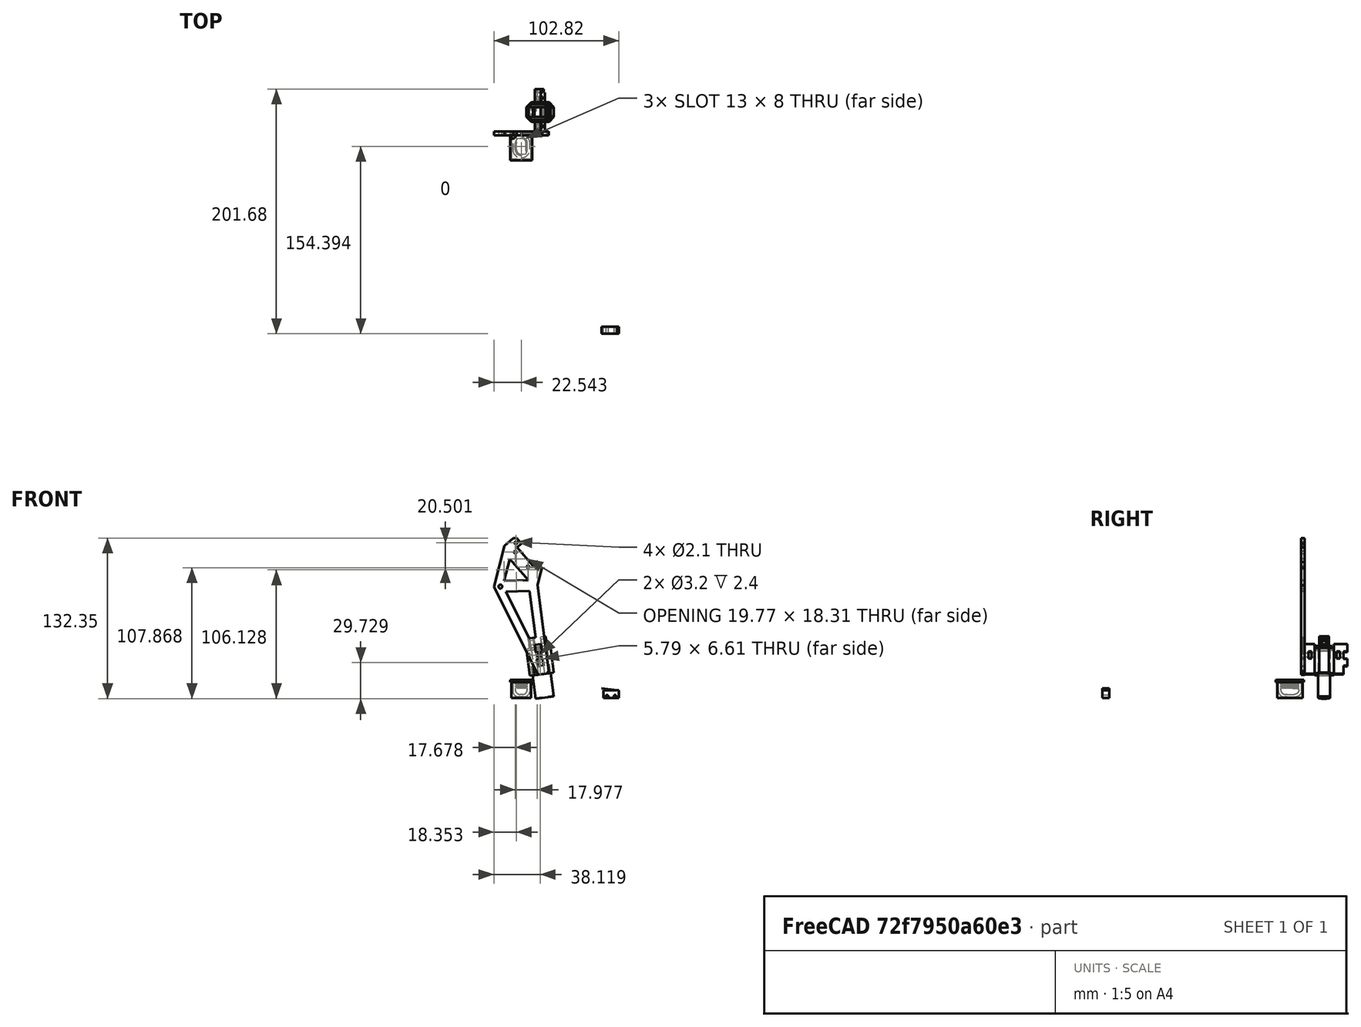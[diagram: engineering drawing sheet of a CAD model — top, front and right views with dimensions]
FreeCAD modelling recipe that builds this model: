
FCSTD DOCUMENT  (FreeCAD 0.19R24276 (Git))
Label: leg_redesigned
License: All rights reserved
LicenseURL: http://en.wikipedia.org/wiki/All_rights_reserved
objects: Sketcher::SketchObject×40, PartDesign::Pocket×30, PartDesign::Pad×19, PartDesign::Chamfer×10, PartDesign::Body×7, PartDesign::Plane×7, PartDesign::ShapeBinder×6, PartDesign::Fillet×6, Mesh::Feature×5, Part::Feature×4, PartDesign::FeatureBase×1
note: 195 computed .brp shape members not serialized (recipe doc carries the construction recipe); baked Part::Feature solids carry a one-line shape summary decoded from their .brp

FEATURE [Mesh::Feature] Component003  label="left_part_original"
FEATURE [Mesh::Feature] Component004  label="right_part_original"
FEATURE [Mesh::Feature] Component005  label="mid_part_original"
FEATURE [Part::Feature] Component004001  label="right_part_original_shape"
  shape: bbox 45.1 x 3 x 112.7 mm, 1032 faces, 0 solids (baked)
FEATURE [Part::Feature] Component003001  label="left_part_original_shape"
  shape: bbox 45.1 x 3 x 112.7 mm, 1032 faces, 0 solids (baked)
FEATURE [PartDesign::ShapeBinder] ShapeBinder
  Support = -> [Component004001]
  TraceSupport = false
FEATURE [PartDesign::ShapeBinder] ShapeBinder001
  Support = -> [Component004001]
  TraceSupport = false
FEATURE [PartDesign::ShapeBinder] ShapeBinder002
  Support = -> [Component003001]
  TraceSupport = false
FEATURE [Sketcher::SketchObject] Sketch
  ExternalGeometry = -> [ShapeBinder,ShapeBinder001,ShapeBinder002]
  FullyConstrained = true
  MapMode = 5
  Placement = pos=(-44.9291,5e-16,-5.90422) rot=(-0.600901,0.600901,0.527102;4.11178rad)
  Support = -> [ShapeBinder]
  sketch-geometry (18):
    g0: LineSegment StartX=-198.684 StartY=38.8278 StartZ=0 EndX=-201.684 EndY=38.8278 EndZ=0
    g1: LineSegment StartX=-198.684 StartY=38.8278 StartZ=0 EndX=-198.684 EndY=44.8278 EndZ=0
    g2: LineSegment StartX=-198.684 StartY=44.8278 StartZ=0 EndX=-201.684 EndY=44.8278 EndZ=0
    g3: LineSegment StartX=-201.684 StartY=44.8278 StartZ=0 EndX=-201.684 EndY=50.8278 EndZ=0
    g4: LineSegment StartX=-201.684 StartY=50.8278 StartZ=0 EndX=-198.684 EndY=50.8278 EndZ=0
    g5: LineSegment StartX=-198.684 StartY=50.8278 StartZ=0 EndX=-166.684 EndY=50.8278 EndZ=0
    g6: LineSegment StartX=-166.684 StartY=50.8278 StartZ=0 EndX=-163.684 EndY=50.8278 EndZ=0
    g7: LineSegment StartX=-163.684 StartY=50.8278 StartZ=0 EndX=-163.684 EndY=44.8278 EndZ=0
    g8: LineSegment StartX=-163.684 StartY=44.8278 StartZ=0 EndX=-166.684 EndY=44.8278 EndZ=0
    g9: LineSegment StartX=-166.684 StartY=44.8278 StartZ=0 EndX=-166.684 EndY=38.8278 EndZ=0
    g10: LineSegment StartX=-166.684 StartY=38.8278 StartZ=0 EndX=-163.684 EndY=38.8278 EndZ=0
    g11: LineSegment StartX=-163.684 StartY=38.8278 StartZ=0 EndX=-163.684 EndY=32.8278 EndZ=0
    g12: LineSegment StartX=-163.684 StartY=32.8278 StartZ=0 EndX=-166.684 EndY=32.8278 EndZ=0
    g13: LineSegment StartX=-201.684 StartY=32.8278 StartZ=0 EndX=-201.684 EndY=38.8278 EndZ=0
    g14: LineSegment StartX=-166.684 StartY=32.8278 StartZ=0 EndX=-166.684 EndY=26.1412 EndZ=0
    g15: LineSegment StartX=-166.684 StartY=26.1412 StartZ=0 EndX=-198.684 EndY=26.1412 EndZ=0
    g16: LineSegment StartX=-198.684 StartY=26.1412 StartZ=0 EndX=-198.684 EndY=32.8278 EndZ=0
    g17: LineSegment StartX=-201.684 StartY=32.8278 StartZ=0 EndX=-198.684 EndY=32.8278 EndZ=0
  constraints (40):
    c: Coincident(g0,g-3)
    c: Coincident(g0,g-4)
    c: Coincident(g1,g0)
    c: Coincident(g1,g-5)
    c: Coincident(g2,g-6)
    c: Coincident(g3,g2)
    c: Vertical(g3)
    c: Coincident(g4,g3)
    c: Coincident(g4,g-6)
    c: Horizontal(g4)
    c: Coincident(g5,g4)
    c: Coincident(g5,g-10)
    c: Coincident(g6,g5)
    c: Coincident(g6,g-9)
    c: Coincident(g7,g6)
    c: Vertical(g7)
    c: Coincident(g8,g7)
    c: Coincident(g8,g-10)
    c: Horizontal(g8)
    c: Coincident(g9,g8)
    c: Coincident(g9,g-8)
    c: Coincident(g10,g9)
    c: Coincident(g10,g-7)
    c: Coincident(g11,g10)
    c: Vertical(g11)
    c: Coincident(g12,g11)
    c: Horizontal(g12)
    c: Coincident(g12,g-8)
    c: Coincident(g13,g0)
    c: Coincident(g1,g2)
    c: Coincident(g14,g12)
    c: Coincident(g15,g14)
    c: Coincident(g-12,g14)
    c: Coincident(g-11,g15)
    c: Coincident(g16,g15)
    c: Vertical(g16)
    c: Coincident(g17,g13)
    c: Horizontal(g17)
    c: Coincident(g16,g17)
    c: Coincident(g-4,g13)
FEATURE [PartDesign::Pad] Pad
  Direction = (1,1,1)
  Length = 5
  Length2 = 100
  Profile = -> Sketch
  Type = 0
FEATURE [Sketcher::SketchObject] Sketch002
  ExternalGeometry = -> [Pad]
  FullyConstrained = true
  MapMode = 5
  Placement = pos=(-6.62244,0,50.3945) rot=(0,-1,0;0.130663rad)
  Support = -> [Pad]
  sketch-geometry (8):
    g0: GeomPoint X=-45.3154 Y=182.684 Z=0
    g1: LineSegment StartX=-57.8154 StartY=190.684 StartZ=0 EndX=-37.8154 EndY=190.684 EndZ=0
    g2: LineSegment StartX=-37.8154 StartY=190.684 StartZ=0 EndX=-37.8154 EndY=174.684 EndZ=0
    g3: LineSegment StartX=-37.8154 StartY=174.684 StartZ=0 EndX=-57.8154 EndY=174.684 EndZ=0
    g4: LineSegment StartX=-57.8154 StartY=174.684 StartZ=0 EndX=-57.8154 EndY=190.684 EndZ=0
    g5: LineSegment StartX=-50.3154 StartY=174.684 StartZ=0 EndX=-45.3154 EndY=174.684 EndZ=0
    g6: GeomPoint X=-47.8154 Y=174.684 Z=0
    g7: LineSegment StartX=-45.3154 StartY=182.684 StartZ=0 EndX=-37.8154 EndY=182.684 EndZ=0
  constraints (19):
    c: Symmetric(g-7,g-10,g0)
    c: Coincident(g1,g2)
    c: Coincident(g2,g3)
    c: Coincident(g3,g4)
    c: Coincident(g4,g1)
    c: Horizontal(g1)
    c: Vertical(g2)
    c: Vertical(g4)
    c: PointOnObject(g5,g-3)
    c: PointOnObject(g5,g-4)
    c: Symmetric(g5,g5,g6)
    c: Symmetric(g3,g2,g6)
    c: Perpendicular(g-3,g5)
    c: Perpendicular(g-3,g3)
    c: Coincident(g7,g0)
    c: Horizontal(g7)
    c: Symmetric(g1,g2,g7)
    c: DistanceX(g1,g1) = 20
    c: DistanceY(g2,g2) = 16
FEATURE [PartDesign::Pad] Pad001
  BaseFeature = -> Pad
  Direction = (1,1,1)
  Length = 24.68
  Length2 = 100
  Profile = -> Sketch002
  Reversed = true
  Type = 0
FEATURE [Sketcher::SketchObject] Sketch003
  ExternalGeometry = -> [Pad001]
  FullyConstrained = true
  MapMode = 5
  Placement = pos=(-6.62244,0,50.3945) rot=(0,-1,0;0.130663rad)
  Support = -> [Pad001]
  sketch-geometry (6):
    g0: ArcOfCircle CenterX=-50.3154 CenterY=182.684 CenterZ=0 NormalX=0 NormalY=0 NormalZ=1 AngleXU=0 Radius=5.2 StartAngle=1.59003 EndAngle=4.71239
    g1: ArcOfCircle CenterX=-45.2144 CenterY=182.684 CenterZ=0 NormalX=0 NormalY=0 NormalZ=1 AngleXU=0 Radius=5.2 StartAngle=4.71239 EndAngle=7.85417
    g2: LineSegment StartX=-50.3154 StartY=177.484 StartZ=0 EndX=-45.2144 EndY=177.484 EndZ=0
    g3: LineSegment StartX=-50.4154 StartY=187.883 StartZ=0 EndX=-45.2154 EndY=187.884 EndZ=0
    g4: LineSegment StartX=-50.3154 StartY=187.883 StartZ=0 EndX=-45.3154 EndY=187.883 EndZ=0
    g5: GeomPoint X=-47.8154 Y=187.883 Z=0
  constraints (14):
    c: Tangent(g0,g2) = -1.5708
    c: Tangent(g2,g1) = -1.5708
    c: Tangent(g3,g1) = 1.5708
    c: Horizontal(g2)
    c: Equal(g0,g1)
    c: DistanceX(g3,g3) = 5.2
    c: Radius(g0) = 5.2
    c: Symmetric(g-9,g-9,g0)
    c: Coincident(g3,g0)
    c: Horizontal(g4)
    c: PointOnObject(g4,g-9)
    c: PointOnObject(g4,g-10)
    c: Symmetric(g4,g4,g5)
    c: Symmetric(g0,g1,g5)
FEATURE [PartDesign::Pocket] Pocket
  BaseFeature = -> Pad001
  Length = 5
  Length2 = 100
  Profile = -> Sketch003
  Type = 1
FEATURE [Sketcher::SketchObject] Sketch004
  ExternalGeometry = -> [Pocket]
  FullyConstrained = true
  MapMode = 5
  Placement = pos=(-5.84069,0,44.4457) rot=(0.997867,0,0.065285;3.14159rad)
  Support = -> [Pocket]
  sketch-geometry (2):
    g0: Circle CenterX=-47.8154 CenterY=-177.104 CenterZ=0 NormalX=0 NormalY=0 NormalZ=1 AngleXU=0 Radius=1.6
    g1: LineSegment StartX=-47.8154 StartY=-178.124 StartZ=0 EndX=-47.8154 EndY=-176.084 EndZ=0
  constraints (5):
    c: PointOnObject(g1,g-6)
    c: Perpendicular(g1,g-4)
    c: Symmetric(g1,g1,g0)
    c: Symmetric(g-4,g-5,g1)
    c: Radius(g0) = 1.6
FEATURE [PartDesign::Pocket] Pocket001
  BaseFeature = -> Pocket
  Length = 8
  Length2 = 100
  Profile = -> Sketch004
  Type = 0
FEATURE [Sketcher::SketchObject] Sketch005
  ExternalGeometry = -> [Pocket001]
  FullyConstrained = false
  MapMode = 5
  Placement = pos=(0,198.684,0) rot=(0,0.707107,0.707107;3.14159rad)
  Support = -> [Pocket001]
  sketch-geometry (2):
    g0: Circle CenterX=52.8734 CenterY=35.2392 CenterZ=0 NormalX=0 NormalY=0 NormalZ=1 AngleXU=0 Radius=1.6
    g1: LineSegment StartX=50.3789 StartY=35.567 StartZ=0 EndX=55.3363 EndY=34.9156 EndZ=0
  constraints (5):
    c: Symmetric(g-5,g-6,g1)
    c: PointOnObject(g1,g-4)
    c: Perpendicular(g1,g-4)
    c: PointOnObject(g0,g1)
    c: Radius(g0) = 1.6
FEATURE [PartDesign::Pocket] Pocket002
  BaseFeature = -> Pocket001
  Length = 8
  Length2 = 100
  Profile = -> Sketch005
  Type = 0
FEATURE [Sketcher::SketchObject] Sketch006
  ExternalGeometry = -> [Pocket002]
  FullyConstrained = false
  MapMode = 5
  Placement = pos=(0,174.684,0) rot=(1,0,0;1.5708rad)
  Support = -> [Pocket002]
  sketch-geometry (14):
    g0: LineSegment StartX=-172.397 StartY=37.8156 StartZ=0 EndX=-169.797 EndY=37.8156 EndZ=0
    g1: LineSegment StartX=-169.797 StartY=37.8156 StartZ=0 EndX=-169.797 EndY=32.0156 EndZ=0
    g2: LineSegment StartX=-169.797 StartY=32.0156 StartZ=0 EndX=-172.397 EndY=32.0156 EndZ=0
    g3: LineSegment StartX=-172.397 StartY=32.0156 StartZ=0 EndX=-172.397 EndY=37.8156 EndZ=0
    g4: LineSegment StartX=-52.7272 StartY=37.8156 StartZ=0 EndX=-50.1272 EndY=37.8156 EndZ=0
    g5: LineSegment StartX=-50.1272 StartY=37.8156 StartZ=0 EndX=-50.1272 EndY=32.0156 EndZ=0
    g6: LineSegment StartX=-50.1272 StartY=32.0156 StartZ=0 EndX=-52.7272 EndY=32.0156 EndZ=0
    g7: LineSegment StartX=-52.7272 StartY=32.0156 StartZ=0 EndX=-52.7272 EndY=37.8156 EndZ=0
    g8: GeomPoint X=87.0771 Y=37.8156 Z=0
    g9: GeomPoint X=-309.601 Y=37.8156 Z=0
    g10: LineSegment StartX=87.0771 StartY=37.8156 StartZ=0 EndX=-309.601 EndY=37.8156 EndZ=0
    g11: GeomPoint X=-111.262 Y=37.8156 Z=0
    g12: GeomPoint X=-55.3363 Y=34.9156 Z=0
    g13: GeomPoint X=-52.7272 Y=34.9156 Z=0
  constraints (31):
    c: Coincident(g0,g1)
    c: Coincident(g1,g2)
    c: Coincident(g2,g3)
    c: Coincident(g3,g0)
    c: Horizontal(g0)
    c: Horizontal(g2)
    c: Vertical(g1)
    c: Vertical(g3)
    c: Coincident(g4,g5)
    c: Coincident(g5,g6)
    c: Coincident(g6,g7)
    c: Coincident(g7,g4)
    c: Horizontal(g4)
    c: Horizontal(g6)
    c: Vertical(g5)
    c: Vertical(g7)
    c: DistanceX(g4,g4) = 2.6
    c: DistanceY(g5,g5) = 5.8
    c: Equal(g0,g4)
    c: Equal(g1,g5)
    c: Horizontal(g2,g5)
    c: PointOnObject(g8,g-7)
    c: DistanceX(g-9,g4) = 3
    c: Coincident(g10,g8)
    c: Coincident(g10,g9)
    c: Horizontal(g10)
    c: Symmetric(g8,g9,g11)
    c: Symmetric(g4,g0,g11)
    c: Symmetric(g-9,g-10,g12)
    c: Symmetric(g4,g6,g13)
    c: Horizontal(g12,g13)
FEATURE [PartDesign::Pocket] Pocket003
  BaseFeature = -> Pocket002
  Length = 5
  Length2 = 100
  Profile = -> Sketch006
  Type = 1
FEATURE [PartDesign::Chamfer] Chamfer
  Angle = 45
  Base = -> Pocket003 [Edge102,Edge66,Edge77,Edge50]
  BaseFeature = -> Pocket003
  ChamferType = 0
  FlipDirection = false
  Size = 4
  Size2 = 1
  SupportTransform = false
FEATURE [Sketcher::SketchObject] Sketch008
  FullyConstrained = false
  MapMode = 5
  Placement = pos=(-6.62244,0,50.3945) rot=(0,-1,0;0.130663rad)
  sketch-geometry (11):
    g0: LineSegment StartX=-57.8154 StartY=186.684 StartZ=0 EndX=-53.8154 EndY=190.684 EndZ=0
    g1: LineSegment StartX=-53.8154 StartY=190.684 StartZ=0 EndX=-44.3154 EndY=190.684 EndZ=0
    g2: LineSegment StartX=-44.3154 StartY=190.684 StartZ=0 EndX=-41.8154 EndY=190.684 EndZ=0
    g3: LineSegment StartX=-41.8154 StartY=190.684 StartZ=0 EndX=-37.8154 EndY=186.684 EndZ=0
    g4: LineSegment StartX=-37.8154 StartY=186.684 StartZ=0 EndX=-37.8154 EndY=178.684 EndZ=0
    g5: LineSegment StartX=-37.8154 StartY=178.684 StartZ=0 EndX=-41.8154 EndY=174.684 EndZ=0
    g6: LineSegment StartX=-41.8154 StartY=174.684 StartZ=0 EndX=-44.3154 EndY=174.684 EndZ=0
    g7: LineSegment StartX=-44.3154 StartY=174.684 StartZ=0 EndX=-51.3154 EndY=174.684 EndZ=0
    g8: LineSegment StartX=-51.3154 StartY=174.684 StartZ=0 EndX=-53.8154 EndY=174.684 EndZ=0
    g9: LineSegment StartX=-53.8154 StartY=174.684 StartZ=0 EndX=-57.8154 EndY=178.684 EndZ=0
    g10: LineSegment StartX=-57.8154 StartY=178.684 StartZ=0 EndX=-57.8154 EndY=186.684 EndZ=0
  constraints (11):
    c: Coincident(g1,g0)
    c: Coincident(g3,g2)
    c: Coincident(g4,g3)
    c: Coincident(g5,g4)
    c: Coincident(g6,g5)
    c: Coincident(g7,g6)
    c: Coincident(g9,g8)
    c: Coincident(g10,g0)
    c: Coincident(g2,g1)
    c: Coincident(g10,g9)
    c: Coincident(g8,g7)
FEATURE [PartDesign::Pocket] Pocket004
  BaseFeature = -> Chamfer
  Length = 4
  Length2 = 100
  Profile = -> Sketch008
  Type = 0
FEATURE [PartDesign::ShapeBinder] ShapeBinder003
  Support = -> [Pocket004]
  TraceSupport = false
FEATURE [Sketcher::SketchObject] Sketch009
  ExternalGeometry = -> [ShapeBinder003]
  FullyConstrained = true
  MapMode = 5
  Placement = pos=(-6.10127,5e-16,46.4286) rot=(0,-1,0;0.130663rad)
  Support = -> [ShapeBinder003]
  sketch-geometry (4):
    g0: ArcOfCircle CenterX=-50.3154 CenterY=182.684 CenterZ=0 NormalX=0 NormalY=0 NormalZ=1 AngleXU=0 Radius=5 StartAngle=1.5708 EndAngle=4.71239
    g1: ArcOfCircle CenterX=-45.3154 CenterY=182.684 CenterZ=0 NormalX=0 NormalY=0 NormalZ=1 AngleXU=0 Radius=5 StartAngle=4.71239 EndAngle=7.85398
    g2: LineSegment StartX=-50.3154 StartY=177.684 StartZ=0 EndX=-45.3154 EndY=177.684 EndZ=0
    g3: LineSegment StartX=-50.3154 StartY=187.684 StartZ=0 EndX=-45.3154 EndY=187.684 EndZ=0
  constraints (7):
    c: Tangent(g0,g3) = 1.5708
    c: Tangent(g0,g2) = -1.5708
    c: Tangent(g2,g1) = -1.5708
    c: Tangent(g3,g1) = 1.5708
    c: Horizontal(g2)
    c: Coincident(g0,g-4)
    c: Tangent(g1,g-3) = -1.5708
FEATURE [PartDesign::Pad] Pad002
  Direction = (1,1,1)
  Length = 40
  Length2 = 100
  Profile = -> Sketch009
  Reversed = true
  Type = 0
FEATURE [Sketcher::SketchObject] Sketch010
  ExternalGeometry = -> [Pad002,ShapeBinder003]
  FullyConstrained = false
  MapMode = 5
  Placement = pos=(-6.10127,-4.7e-15,46.4286) rot=(0,-1,0;0.130663rad)
  Support = -> [Pad002]
  sketch-geometry (15):
    g0: LineSegment StartX=-50.3154 StartY=182.684 StartZ=0 EndX=-45.3154 EndY=182.684 EndZ=0
    g1: GeomPoint X=-47.8154 Y=182.684 Z=0
    g2: LineSegment StartX=-56.3654 StartY=186.012 StartZ=0 EndX=-53.1441 EndY=189.234 EndZ=0
    g3: LineSegment StartX=-53.1441 StartY=189.234 StartZ=0 EndX=-42.4867 EndY=189.234 EndZ=0
    g4: LineSegment StartX=-42.4867 StartY=189.234 StartZ=0 EndX=-39.2654 EndY=186.012 EndZ=0
    g5: LineSegment StartX=-39.2654 StartY=186.012 StartZ=0 EndX=-39.2654 EndY=179.355 EndZ=0
    g6: LineSegment StartX=-39.2654 StartY=179.355 StartZ=0 EndX=-42.4867 EndY=176.134 EndZ=0
    g7: LineSegment StartX=-42.4867 StartY=176.134 StartZ=0 EndX=-53.1441 EndY=176.134 EndZ=0
    g8: LineSegment StartX=-53.1441 StartY=176.134 StartZ=0 EndX=-56.3654 EndY=179.355 EndZ=0
    g9: LineSegment StartX=-56.3654 StartY=179.355 StartZ=0 EndX=-56.3654 EndY=186.012 EndZ=0
    g10: LineSegment StartX=-47.8154 StartY=190.684 StartZ=0 EndX=-47.8154 EndY=174.684 EndZ=0
    g11: LineSegment StartX=-56.3654 StartY=182.684 StartZ=0 EndX=-39.2654 EndY=182.684 EndZ=0
    g12: GeomPoint X=-47.8154 Y=189.234 Z=0
    g13: GeomPoint X=-47.8154 Y=176.134 Z=0
    g14: LineSegment StartX=-40.8761 StartY=187.623 StartZ=0 EndX=-39.8154 EndY=188.684 EndZ=0
  constraints (37):
    c: Symmetric(g-3,g-4,g1)
    c: Coincident(g3,g2)
    c: Horizontal(g3)
    c: Coincident(g5,g4)
    c: Vertical(g5)
    c: Horizontal(g7)
    c: Coincident(g9,g2)
    c: Vertical(g9)
    c: Equal(g3,g7)
    c: Coincident(g7,g8)
    c: Coincident(g6,g7)
    c: Coincident(g4,g3)
    c: Coincident(g6,g5)
    c: Coincident(g8,g9)
    c: Equal(g2,g4)
    c: Equal(g4,g6)
    c: Equal(g6,g8)
    c: Equal(g9,g5)
    c: Horizontal(g4,g2)
    c: Vertical(g10)
    c: Horizontal(g11)
    c: PointOnObject(g11,g5)
    c: PointOnObject(g11,g9)
    c: Symmetric(g11,g11,g1)
    c: PointOnObject(g10,g-19)
    c: PointOnObject(g10,g-16)
    c: PointOnObject(g13,g7)
    c: PointOnObject(g12,g3)
    c: PointOnObject(g13,g10)
    c: PointOnObject(g12,g10)
    c: Symmetric(g12,g13,g1)
    c: Distance(g4,g-14) = 1.5
    c: Distance(g3,g-14) = 1.5
    c: Symmetric(g-14,g-15,g14)
    c: Symmetric(g3,g4,g14)
    c: Perpendicular(g14,g4)
    c: Distance(g2,g-17) = 1.45
FEATURE [PartDesign::Pad] Pad003
  BaseFeature = -> Pad002
  Direction = (1,1,1)
  Length = 2
  Length2 = 100
  Profile = -> Sketch010
  Type = 0
FEATURE [Mesh::Feature] slider_legacy
FEATURE [Part::Feature] slider_legacy001
  shape: bbox 17.12 x 15 x 43.92 mm, 7930 faces, 0 solids (baked)
FEATURE [Sketcher::SketchObject] Sketch011
  ExternalGeometry = -> [ShapeBinder003]
  FullyConstrained = true
  MapMode = 5
  Placement = pos=(-6.36185,-4.4e-15,48.4116) rot=(0,-1,0;0.130663rad)
  Support = -> [Pad003]
  sketch-geometry (21):
    g0: LineSegment StartX=-50.9654 StartY=186.684 StartZ=0 EndX=-50.9654 EndY=178.684 EndZ=0
    g1: LineSegment StartX=-44.6654 StartY=186.684 StartZ=0 EndX=-44.6654 EndY=178.684 EndZ=0
    g2: LineSegment StartX=-44.6654 StartY=186.684 StartZ=0 EndX=-41.6654 EndY=186.684 EndZ=0
    g3: LineSegment StartX=-44.6654 StartY=178.684 StartZ=0 EndX=-41.6654 EndY=178.684 EndZ=0
    g4: LineSegment StartX=-50.9654 StartY=178.684 StartZ=0 EndX=-53.9654 EndY=178.684 EndZ=0
    g5: LineSegment StartX=-50.9654 StartY=186.684 StartZ=0 EndX=-53.9654 EndY=186.684 EndZ=0
    g6: LineSegment StartX=-47.8154 StartY=190.684 StartZ=0 EndX=-47.8154 EndY=174.684 EndZ=0
    g7: LineSegment StartX=-57.8154 StartY=182.684 StartZ=0 EndX=-37.8154 EndY=182.684 EndZ=0
    g8: GeomPoint X=-47.8154 Y=182.684 Z=0
    g9: GeomPoint X=-47.8154 Y=182.684 Z=0
    g10: GeomPoint X=-44.6654 Y=182.684 Z=0
    g11: GeomPoint X=-47.8154 Y=186.684 Z=0
    g12: ArcOfCircle CenterX=-52.9799 CenterY=184.943 CenterZ=0 NormalX=0 NormalY=0 NormalZ=1 AngleXU=0 Radius=2 StartAngle=2.08605 EndAngle=3.02113
    g13: ArcOfCircle CenterX=-52.9799 CenterY=180.424 CenterZ=0 NormalX=0 NormalY=0 NormalZ=1 AngleXU=0 Radius=2 StartAngle=3.26205 EndAngle=4.19714
    g14: LineSegment StartX=-54.9654 StartY=185.184 StartZ=0 EndX=-54.9654 EndY=180.184 EndZ=0
    g15: GeomPoint X=-54.9654 Y=182.684 Z=0
    g16: GeomPoint X=-54.9654 Y=185.184 Z=0
    g17: GeomPoint X=-54.9654 Y=180.184 Z=0
    g18: LineSegment StartX=-40.6654 StartY=185.184 StartZ=0 EndX=-40.6654 EndY=180.184 EndZ=0
    g19: ArcOfCircle CenterX=-42.6509 CenterY=184.943 CenterZ=0 NormalX=0 NormalY=0 NormalZ=1 AngleXU=0 Radius=2 StartAngle=0.12046 EndAngle=1.05555
    g20: ArcOfCircle CenterX=-42.6509 CenterY=180.424 CenterZ=0 NormalX=0 NormalY=0 NormalZ=1 AngleXU=0 Radius=2 StartAngle=5.22764 EndAngle=6.16273
  constraints (53):
    c: Vertical(g0)
    c: Vertical(g1)
    c: Equal(g0,g1)
    c: Horizontal(g1,g0)
    c: DistanceX(g0,g1) = 6.3
    c: Distance(g0) = 8
    c: Coincident(g2,g1)
    c: Horizontal(g2)
    c: Coincident(g3,g1)
    c: Coincident(g4,g0)
    c: Horizontal(g4)
    c: Coincident(g5,g0)
    c: Horizontal(g5)
    c: Horizontal(g3)
    c: Equal(g4,g5)
    c: Equal(g5,g2)
    c: Equal(g2,g3)
    c: DistanceX(g4,g4) = 3
    c: Vertical(g6)
    c: Horizontal(g7)
    c: PointOnObject(g7,g-3)
    c: PointOnObject(g6,g-6)
    c: Symmetric(g7,g7,g9)
    c: Symmetric(g6,g6,g8)
    c: Symmetric(g-4,g-4,g7)
    c: Symmetric(g-5,g-5,g6)
    c: Symmetric(g1,g1,g10)
    c: PointOnObject(g10,g7)
    c: Symmetric(g0,g1,g11)
    c: PointOnObject(g11,g6)
    c: Coincident(g12,g5)
    c: Coincident(g13,g4)
    c: Vertical(g13,g12)
    c: Equal(g13,g12)
    c: Coincident(g14,g12)
    c: Coincident(g14,g13)
    c: PointOnObject(g15,g7)
    c: Coincident(g16,g12)
    c: Coincident(g17,g13)
    c: Symmetric(g12,g13,g15)
    c: DistanceX(g12,g5) = 1
    c: Vertical(g18)
    c: Coincident(g19,g2)
    c: Coincident(g19,g18)
    c: Coincident(g20,g3)
    c: Coincident(g20,g18)
    c: Horizontal(g18,g13)
    c: Horizontal(g18,g12)
    c: Equal(g12,g19)
    c: Equal(g19,g20)
    c: DistanceY(g14,g14) = 5
    c: DistanceX(g2,g18) = 1
    c: Radius(g12) = 2
FEATURE [PartDesign::Pad] Pad004
  BaseFeature = -> Pad003
  Direction = (1,1,1)
  Length = 8
  Length2 = 100
  Profile = -> Sketch011
  Type = 0
FEATURE [Sketcher::SketchObject] Sketch012
  ExternalGeometry = -> [Pad004]
  FullyConstrained = false
  MapMode = 5
  Placement = pos=(-54.4969,5e-16,-7.16153) rot=(-0.600901,0.600901,0.527102;4.11178rad)
  Support = -> [Pad004]
  sketch-geometry (2):
    g0: ArcOfCircle CenterX=-182.684 CenterY=54.8751 CenterZ=0 NormalX=0 NormalY=0 NormalZ=1 AngleXU=0 Radius=6.54374 StartAngle=4.32038 EndAngle=5.1044
    g1: LineSegment StartX=-185.184 StartY=48.8278 StartZ=0 EndX=-180.184 EndY=48.8278 EndZ=0
  constraints (4):
    c: Coincident(g0,g-3)
    c: Coincident(g0,g-3)
    c: Coincident(g1,g0)
    c: Coincident(g1,g0)
FEATURE [PartDesign::Pocket] Pocket005
  BaseFeature = -> Pad004
  Length = 6.3
  Length2 = 100
  Profile = -> Sketch012
  Reversed = true
  Type = 0
FEATURE [Sketcher::SketchObject] Sketch013
  ExternalGeometry = -> [Pocket005]
  FullyConstrained = false
  MapMode = 5
  Placement = pos=(-54.4969,5e-16,-7.16153) rot=(-0.600901,0.600901,0.527102;4.11178rad)
  Support = -> [Pocket005]
  sketch-geometry (5):
    g0: Circle CenterX=-181.888 CenterY=53.2425 CenterZ=0 NormalX=0 NormalY=0 NormalZ=1 AngleXU=0 Radius=1.7
    g1: LineSegment StartX=-186.684 StartY=52.8278 StartZ=0 EndX=-178.684 EndY=52.8278 EndZ=0
    g2: LineSegment StartX=-182.684 StartY=56.8278 StartZ=0 EndX=-182.684 EndY=48.8278 EndZ=0
    g3: GeomPoint X=-182.684 Y=52.8278 Z=0
    g4: GeomPoint X=-182.684 Y=52.8278 Z=0
  constraints (11):
    c: Radius(g0) = 1.7
    c: PointOnObject(g1,g-8)
    c: PointOnObject(g1,g-6)
    c: Horizontal(g1)
    c: PointOnObject(g2,g-5)
    c: PointOnObject(g2,g-7)
    c: Vertical(g2)
    c: Symmetric(g1,g1,g3)
    c: Symmetric(g2,g2,g4)
    c: Coincident(g4,g3)
    c: Coincident(g0)
FEATURE [PartDesign::Pocket] Pocket006
  BaseFeature = -> Pocket005
  Length = 5
  Length2 = 20
  Profile = -> Sketch013
  Type = 4
FEATURE [Sketcher::SketchObject] Sketch014
  ExternalGeometry = -> [Pocket006]
  FullyConstrained = false
  MapMode = 5
  Placement = pos=(-54.4969,1e-15,-7.16153) rot=(0.600901,-0.600901,-0.527102;2.17141rad)
  Support = -> [Pocket006]
  sketch-geometry (1):
    g0: Circle CenterX=-182.684 CenterY=52.8278 CenterZ=0 NormalX=0 NormalY=0 NormalZ=1 AngleXU=0 Radius=3.2
  constraints (1):
    c: Radius(g0) = 3.2
FEATURE [PartDesign::Pocket] Pocket007
  BaseFeature = -> Pocket006
  Length = 1
  Length2 = 100
  Profile = -> Sketch014
  Type = 0
FEATURE [Sketcher::SketchObject] Sketch015
  ExternalGeometry = -> [Pocket007]
  FullyConstrained = true
  MapMode = 5
  Placement = pos=(-40.3187,4e-16,-5.29836) rot=(0.550513,0.550513,0.627591;2.02067rad)
  Support = -> [Pocket007]
  sketch-geometry (7):
    g0: LineSegment StartX=184.329 StartY=55.6778 StartZ=0 EndX=181.038 EndY=55.6778 EndZ=0
    g1: LineSegment StartX=181.038 StartY=55.6778 StartZ=0 EndX=179.393 EndY=52.8278 EndZ=0
    g2: LineSegment StartX=179.393 StartY=52.8278 StartZ=0 EndX=181.038 EndY=49.9778 EndZ=0
    g3: LineSegment StartX=181.038 StartY=49.9778 StartZ=0 EndX=184.329 EndY=49.9778 EndZ=0
    g4: LineSegment StartX=184.329 StartY=49.9778 StartZ=0 EndX=185.975 EndY=52.8278 EndZ=0
    g5: LineSegment StartX=185.975 StartY=52.8278 StartZ=0 EndX=184.329 EndY=55.6778 EndZ=0
    g6: Circle CenterX=182.684 CenterY=52.8278 CenterZ=0 NormalX=0 NormalY=0 NormalZ=1 AngleXU=0 Radius=3.2909
  constraints (16):
    c: Coincident(g0,g1)
    c: Coincident(g1,g2)
    c: Coincident(g2,g3)
    c: Coincident(g3,g4)
    c: Coincident(g4,g5)
    c: Coincident(g5,g0)
    c: Equal(g0, g1-g5) x5
    c: PointOnObject(g0,g6)
    c: PointOnObject(g1,g6)
    c: PointOnObject(g2,g6)
    c: PointOnObject(g3,g6)
    c: PointOnObject(g4,g6)
    c: PointOnObject(g5,g6)
    c: Coincident(g6,g-6)
    c: Parallel(g0,g-4)
    c: Distance(g2,g4) = 5.7
FEATURE [PartDesign::Pocket] Pocket008
  BaseFeature = -> Pocket007
  Length = 1.5
  Length2 = 100
  Profile = -> Sketch015
  Type = 0
FEATURE [Sketcher::SketchObject] Sketch019
  FullyConstrained = false
  MapMode = 5
  Support = -> [XY_Plane003]
  sketch-geometry (4):
    g0: LineSegment StartX=-75.677 StartY=164.969 StartZ=0 EndX=-59.677 EndY=164.969 EndZ=0
    g1: LineSegment StartX=-59.677 StartY=164.969 StartZ=0 EndX=-59.677 EndY=143.969 EndZ=0
    g2: LineSegment StartX=-59.677 StartY=143.969 StartZ=0 EndX=-75.677 EndY=143.969 EndZ=0
    g3: LineSegment StartX=-75.677 StartY=143.969 StartZ=0 EndX=-75.677 EndY=164.969 EndZ=0
  constraints (10):
    c: Coincident(g0,g1)
    c: Coincident(g1,g2)
    c: Coincident(g2,g3)
    c: Coincident(g3,g0)
    c: Horizontal(g0)
    c: Horizontal(g2)
    c: Vertical(g1)
    c: Vertical(g3)
    c: DistanceY(g1,g1) = 21
    c: DistanceX(g0,g0) = 16
FEATURE [PartDesign::Pad] Pad005
  Direction = (1,1,1)
  Length = 14
  Length2 = 100
  Profile = -> Sketch019
  Type = 0
FEATURE [Sketcher::SketchObject] Sketch020
  ExternalGeometry = -> [Pad005]
  FullyConstrained = true
  MapMode = 5
  Placement = pos=(0,0,14) rot=(0,0,1;0rad)
  Support = -> [Pad005]
  sketch-geometry (10):
    g0: ArcOfCircle CenterX=-67.677 CenterY=156.969 CenterZ=0 NormalX=0 NormalY=0 NormalZ=1 AngleXU=0 Radius=5 StartAngle=-1.8e-15 EndAngle=3.14159
    g1: ArcOfCircle CenterX=-67.677 CenterY=151.969 CenterZ=0 NormalX=0 NormalY=0 NormalZ=1 AngleXU=0 Radius=5 StartAngle=3.14159 EndAngle=6.28319
    g2: LineSegment StartX=-72.677 StartY=156.969 StartZ=0 EndX=-72.677 EndY=151.969 EndZ=0
    g3: LineSegment StartX=-62.677 StartY=156.969 StartZ=0 EndX=-62.677 EndY=151.969 EndZ=0
    g4: LineSegment StartX=-67.677 StartY=143.969 StartZ=0 EndX=-67.677 EndY=164.969 EndZ=0
    g5: GeomPoint X=-67.677 Y=154.469 Z=0
    g6: ArcOfCircle CenterX=-67.677 CenterY=156.969 CenterZ=0 NormalX=0 NormalY=0 NormalZ=1 AngleXU=0 Radius=7 StartAngle=-9e-16 EndAngle=3.14159
    g7: ArcOfCircle CenterX=-67.677 CenterY=151.969 CenterZ=0 NormalX=0 NormalY=0 NormalZ=1 AngleXU=0 Radius=7 StartAngle=3.14159 EndAngle=6.28319
    g8: LineSegment StartX=-74.677 StartY=156.969 StartZ=0 EndX=-74.677 EndY=151.969 EndZ=0
    g9: LineSegment StartX=-60.677 StartY=156.969 StartZ=0 EndX=-60.677 EndY=151.969 EndZ=0
  constraints (22):
    c: Tangent(g0,g3) = 1.5708
    c: Tangent(g0,g2) = -1.5708
    c: Tangent(g2,g1) = -1.5708
    c: Tangent(g3,g1) = 1.5708
    c: Vertical(g2)
    c: Equal(g0,g1)
    c: Radius(g0) = 5
    c: DistanceY(g1,g0) = 5
    c: Symmetric(g-6,g-5,g4)
    c: Symmetric(g-6,g-5,g4)
    c: Symmetric(g4,g4,g5)
    c: Symmetric(g0,g1,g5)
    c: Tangent(g6,g9) = 1.5708
    c: Tangent(g6,g8) = -1.5708
    c: Tangent(g8,g7) = -1.5708
    c: Tangent(g9,g7) = 1.5708
    c: Vertical(g8)
    c: Equal(g6,g7)
    c: Horizontal(g7,g1)
    c: Horizontal(g6,g0)
    c: DistanceX(g0,g6) = 2
    c: DistanceX(g7,g1) = 2
FEATURE [PartDesign::Pocket] Pocket012
  BaseFeature = -> Pad005
  Length = 13
  Length2 = 100
  Profile = -> Sketch020
  Type = 0
FEATURE [PartDesign::Fillet] Fillet001
  Base = -> Pocket012 [Edge21,Edge23,Edge19,Edge24]
  BaseFeature = -> Pocket012
  Radius = 5
  SupportTransform = false
FEATURE [PartDesign::Body] Body003  label="mould_female"
  Group = -> [Sketch019,Pad005,Sketch020,Pocket012,Fillet001]
  Origin = -> Origin003
  Tip = -> Fillet001
FEATURE [PartDesign::ShapeBinder] ShapeBinder004
  Support = -> [Fillet001]
  TraceSupport = false
FEATURE [Sketcher::SketchObject] Sketch021
  ExternalGeometry = -> [ShapeBinder004]
  FullyConstrained = true
  MapMode = 5
  Placement = pos=(0,0,14) rot=(0,0,1;0rad)
  Support = -> [ShapeBinder004]
  sketch-geometry (4):
    g0: LineSegment StartX=-76.677 StartY=165.969 StartZ=0 EndX=-58.677 EndY=165.969 EndZ=0
    g1: LineSegment StartX=-58.677 StartY=165.969 StartZ=0 EndX=-58.677 EndY=142.819 EndZ=0
    g2: LineSegment StartX=-58.677 StartY=142.819 StartZ=0 EndX=-76.677 EndY=142.819 EndZ=0
    g3: LineSegment StartX=-76.677 StartY=142.819 StartZ=0 EndX=-76.677 EndY=165.969 EndZ=0
  constraints (12):
    c: Coincident(g0,g1)
    c: Coincident(g1,g2)
    c: Coincident(g2,g3)
    c: Coincident(g3,g0)
    c: Horizontal(g0)
    c: Horizontal(g2)
    c: Vertical(g1)
    c: Vertical(g3)
    c: DistanceY(g-4,g0) = 1
    c: DistanceX(g0,g-4) = 1
    c: DistanceX(g-5,g0) = 1
    c: DistanceY(g1,g-6) = 1.15
FEATURE [PartDesign::Pad] Pad006
  Direction = (1,1,1)
  Length = 1
  Length2 = 100
  Profile = -> Sketch021
  Type = 0
FEATURE [Sketcher::SketchObject] Sketch022
  ExternalGeometry = -> [Pad006]
  FullyConstrained = true
  MapMode = 5
  Placement = pos=(0,0,14) rot=(1,0,0;3.14159rad)
  Support = -> [Pad006]
  sketch-geometry (8):
    g0: LineSegment StartX=-75.677 StartY=-143.819 StartZ=0 EndX=-59.677 EndY=-143.819 EndZ=0
    g1: LineSegment StartX=-59.677 StartY=-143.819 StartZ=0 EndX=-59.677 EndY=-164.969 EndZ=0
    g2: LineSegment StartX=-59.677 StartY=-164.969 StartZ=0 EndX=-75.677 EndY=-164.969 EndZ=0
    g3: LineSegment StartX=-75.677 StartY=-164.969 StartZ=0 EndX=-75.677 EndY=-143.819 EndZ=0
    g4: LineSegment StartX=-76.677 StartY=-142.819 StartZ=0 EndX=-58.677 EndY=-142.819 EndZ=0
    g5: LineSegment StartX=-58.677 StartY=-142.819 StartZ=0 EndX=-58.677 EndY=-165.969 EndZ=0
    g6: LineSegment StartX=-58.677 StartY=-165.969 StartZ=0 EndX=-76.677 EndY=-165.969 EndZ=0
    g7: LineSegment StartX=-76.677 StartY=-165.969 StartZ=0 EndX=-76.677 EndY=-142.819 EndZ=0
  constraints (22):
    c: Coincident(g0,g1)
    c: Coincident(g1,g2)
    c: Coincident(g2,g3)
    c: Coincident(g3,g0)
    c: Horizontal(g0)
    c: Horizontal(g2)
    c: Vertical(g1)
    c: Vertical(g3)
    c: DistanceX(g-4,g0) = 1
    c: DistanceY(g0,g-4) = 1
    c: DistanceY(g-6,g1) = 1
    c: DistanceX(g1,g-6) = 1
    c: Coincident(g4,g5)
    c: Coincident(g5,g6)
    c: Coincident(g6,g7)
    c: Coincident(g7,g4)
    c: Horizontal(g4)
    c: Horizontal(g6)
    c: Vertical(g5)
    c: Vertical(g7)
    c: Coincident(g-6,g5)
    c: Coincident(g4,g-4)
FEATURE [PartDesign::Pad] Pad007
  BaseFeature = -> Pad006
  Direction = (1,1,1)
  Length = 1
  Length2 = 100
  Profile = -> Sketch022
  Type = 0
FEATURE [Sketcher::SketchObject] Sketch023
  ExternalGeometry = -> [Pad007]
  FullyConstrained = false
  MapMode = 5
  Placement = pos=(0,0,14) rot=(1,0,0;3.14159rad)
  Support = -> [Pad007]
  sketch-geometry (4):
    g0: GeomPoint X=-75.677 Y=-164.969 Z=0
    g1: ArcOfCircle CenterX=-75.677 CenterY=-164.969 CenterZ=0 NormalX=0 NormalY=0 NormalZ=1 AngleXU=0 Radius=5.19362 StartAngle=2.03e-14 EndAngle=1.5708
    g2: LineSegment StartX=-75.677 StartY=-159.775 StartZ=0 EndX=-75.677 EndY=-164.969 EndZ=0
    g3: LineSegment StartX=-75.677 StartY=-164.969 StartZ=0 EndX=-70.4834 EndY=-164.969 EndZ=0
  constraints (8):
    c: Coincident(g0,g-4)
    c: Coincident(g1,g0)
    c: PointOnObject(g1,g-3)
    c: PointOnObject(g1,g-4)
    c: Coincident(g2,g1)
    c: Coincident(g2,g1)
    c: Coincident(g3,g1)
    c: Coincident(g3,g1)
FEATURE [Sketcher::SketchObject] Sketch024
  ExternalGeometry = -> [Pad006]
  FullyConstrained = true
  MapMode = 5
  Placement = pos=(0,0,14) rot=(1,0,0;3.14159rad)
  sketch-geometry (6):
    g0: ArcOfCircle CenterX=-67.677 CenterY=-151.894 CenterZ=0 NormalX=0 NormalY=0 NormalZ=1 AngleXU=0 Radius=5 StartAngle=-9e-16 EndAngle=3.14159
    g1: ArcOfCircle CenterX=-67.677 CenterY=-156.894 CenterZ=0 NormalX=0 NormalY=0 NormalZ=1 AngleXU=0 Radius=5 StartAngle=3.14159 EndAngle=6.28319
    g2: LineSegment StartX=-72.677 StartY=-151.894 StartZ=0 EndX=-72.677 EndY=-156.894 EndZ=0
    g3: LineSegment StartX=-62.677 StartY=-151.894 StartZ=0 EndX=-62.677 EndY=-156.894 EndZ=0
    g4: LineSegment StartX=-67.677 StartY=-142.819 StartZ=0 EndX=-67.677 EndY=-165.969 EndZ=0
    g5: GeomPoint X=-67.677 Y=-154.394 Z=0
  constraints (12):
    c: Tangent(g0,g3) = 1.5708
    c: Tangent(g0,g2) = -1.5708
    c: Tangent(g2,g1) = -1.5708
    c: Tangent(g3,g1) = 1.5708
    c: Vertical(g2)
    c: Equal(g0,g1)
    c: DistanceY(g2,g2) = 5
    c: DistanceX(g0,g0) = 10
    c: Symmetric(g-6,g-6,g4)
    c: Symmetric(g-5,g-4,g4)
    c: Symmetric(g0,g1,g5)
    c: Symmetric(g4,g4,g5)
FEATURE [PartDesign::Pad] Pad008
  BaseFeature = -> Pad007
  Direction = (1,1,1)
  Length = 11
  Length2 = 100
  Profile = -> Sketch024
  Type = 0
FEATURE [PartDesign::Plane] DatumPlane003
  AttachmentOffset = pos=(0,0,-5) rot=(0,0,1;0rad)
  Length = 129.546
  MapMode = 5
  Placement = pos=(0,0,8) rot=(1,0,0;3.14159rad)
  ResizeMode = 0
  Width = 218.838
FEATURE [Sketcher::SketchObject] Sketch025
  FullyConstrained = false
  MapMode = 5
  Placement = pos=(0,0,8) rot=(1,0,0;3.14159rad)
  Support = -> [DatumPlane003]
  sketch-geometry (8):
    g0: ArcOfCircle CenterX=-67.677 CenterY=-156.894 CenterZ=0 NormalX=0 NormalY=0 NormalZ=1 AngleXU=0 Radius=4 StartAngle=3.14159 EndAngle=6.28319
    g1: ArcOfCircle CenterX=-67.677 CenterY=-151.894 CenterZ=0 NormalX=0 NormalY=0 NormalZ=1 AngleXU=0 Radius=4 StartAngle=-1.8e-15 EndAngle=3.14159
    g2: LineSegment StartX=-63.677 StartY=-156.894 StartZ=0 EndX=-63.677 EndY=-151.894 EndZ=0
    g3: LineSegment StartX=-71.677 StartY=-156.894 StartZ=0 EndX=-71.677 EndY=-151.894 EndZ=0
    g4: ArcOfCircle CenterX=-67.677 CenterY=-151.894 CenterZ=0 NormalX=0 NormalY=0 NormalZ=1 AngleXU=0 Radius=5 StartAngle=-9e-16 EndAngle=3.14159
    g5: ArcOfCircle CenterX=-67.677 CenterY=-156.894 CenterZ=0 NormalX=0 NormalY=0 NormalZ=1 AngleXU=0 Radius=5 StartAngle=3.14159 EndAngle=6.28319
    g6: LineSegment StartX=-72.677 StartY=-151.894 StartZ=0 EndX=-72.677 EndY=-156.894 EndZ=0
    g7: LineSegment StartX=-62.677 StartY=-151.894 StartZ=0 EndX=-62.677 EndY=-156.894 EndZ=0
  constraints (11):
    c: Tangent(g0,g3) = 1.5708
    c: Tangent(g0,g2) = -1.5708
    c: Tangent(g2,g1) = -1.5708
    c: Tangent(g3,g1) = 1.5708
    c: Vertical(g2)
    c: Tangent(g4,g7) = 1.5708
    c: Tangent(g4,g6) = -1.5708
    c: Tangent(g6,g5) = -1.5708
    c: Tangent(g7,g5) = 1.5708
    c: Coincident(g4,g1)
    c: Coincident(g5,g0)
FEATURE [PartDesign::Pocket] Pocket014
  BaseFeature = -> Pad008
  Length = 1
  Length2 = 100
  Profile = -> Sketch025
  Type = 0
FEATURE [PartDesign::Plane] DatumPlane004
  AttachmentOffset = pos=(0,0,-7) rot=(0,0,1;0rad)
  Length = 129.546
  MapMode = 5
  Placement = pos=(0,0,10) rot=(1,0,0;3.14159rad)
  ResizeMode = 0
  Support = -> [Pocket014]
  Width = 218.838
FEATURE [Sketcher::SketchObject] Sketch026
  FullyConstrained = false
  MapMode = 5
  Placement = pos=(0,0,10) rot=(1,0,0;3.14159rad)
  Support = -> [DatumPlane004]
  sketch-geometry (8):
    g0: ArcOfCircle CenterX=-67.677 CenterY=-151.894 CenterZ=0 NormalX=0 NormalY=0 NormalZ=1 AngleXU=0 Radius=5 StartAngle=-9e-16 EndAngle=3.14159
    g1: ArcOfCircle CenterX=-67.677 CenterY=-156.894 CenterZ=0 NormalX=0 NormalY=0 NormalZ=1 AngleXU=0 Radius=5 StartAngle=3.14159 EndAngle=6.28319
    g2: LineSegment StartX=-72.677 StartY=-151.894 StartZ=0 EndX=-72.677 EndY=-156.894 EndZ=0
    g3: LineSegment StartX=-62.677 StartY=-151.894 StartZ=0 EndX=-62.677 EndY=-156.894 EndZ=0
    g4: ArcOfCircle CenterX=-67.677 CenterY=-151.894 CenterZ=0 NormalX=0 NormalY=0 NormalZ=1 AngleXU=0 Radius=4 StartAngle=8e-16 EndAngle=3.14159
    g5: ArcOfCircle CenterX=-67.677 CenterY=-156.894 CenterZ=0 NormalX=0 NormalY=0 NormalZ=1 AngleXU=0 Radius=4 StartAngle=3.14159 EndAngle=6.28319
    g6: LineSegment StartX=-71.677 StartY=-151.894 StartZ=0 EndX=-71.677 EndY=-156.894 EndZ=0
    g7: LineSegment StartX=-63.677 StartY=-151.894 StartZ=0 EndX=-63.677 EndY=-156.894 EndZ=0
  constraints (12):
    c: Tangent(g0,g3) = 1.5708
    c: Tangent(g0,g2) = -1.5708
    c: Tangent(g2,g1) = -1.5708
    c: Tangent(g3,g1) = 1.5708
    c: Tangent(g4,g7) = 1.5708
    c: Tangent(g4,g6) = -1.5708
    c: Tangent(g6,g5) = -1.5708
    c: Tangent(g7,g5) = 1.5708
    c: Vertical(g6)
    c: Coincident(g4,g0)
    c: Coincident(g5,g1)
    c: DistanceX(g1,g5) = 1
FEATURE [PartDesign::Pocket] Pocket015
  BaseFeature = -> Pocket014
  Length = 1
  Length2 = 100
  Profile = -> Sketch026
  Type = 0
FEATURE [PartDesign::Plane] DatumPlane005
  AttachmentOffset = pos=(0,0,-9) rot=(0,0,1;0rad)
  Length = 129.546
  MapMode = 5
  Placement = pos=(0,0,12) rot=(1,0,0;3.14159rad)
  ResizeMode = 0
  Support = -> [Pocket015]
  Width = 218.838
FEATURE [Sketcher::SketchObject] Sketch027
  ExternalGeometry = -> [Pocket015]
  FullyConstrained = true
  MapMode = 5
  Placement = pos=(0,0,12) rot=(1,0,0;3.14159rad)
  Support = -> [DatumPlane005]
  sketch-geometry (8):
    g0: ArcOfCircle CenterX=-67.677 CenterY=-151.894 CenterZ=0 NormalX=0 NormalY=0 NormalZ=1 AngleXU=0 Radius=4 StartAngle=3.3e-15 EndAngle=3.14159
    g1: ArcOfCircle CenterX=-67.677 CenterY=-156.894 CenterZ=0 NormalX=0 NormalY=0 NormalZ=1 AngleXU=0 Radius=4 StartAngle=3.14159 EndAngle=6.28319
    g2: LineSegment StartX=-71.677 StartY=-151.894 StartZ=0 EndX=-71.677 EndY=-156.894 EndZ=0
    g3: LineSegment StartX=-63.677 StartY=-151.894 StartZ=0 EndX=-63.677 EndY=-156.894 EndZ=0
    g4: ArcOfCircle CenterX=-67.677 CenterY=-151.894 CenterZ=0 NormalX=0 NormalY=0 NormalZ=1 AngleXU=0 Radius=5 StartAngle=1.7e-15 EndAngle=3.14159
    g5: ArcOfCircle CenterX=-67.677 CenterY=-156.894 CenterZ=0 NormalX=0 NormalY=0 NormalZ=1 AngleXU=0 Radius=5 StartAngle=3.14159 EndAngle=6.28319
    g6: LineSegment StartX=-72.677 StartY=-151.894 StartZ=0 EndX=-72.677 EndY=-156.894 EndZ=0
    g7: LineSegment StartX=-62.677 StartY=-151.894 StartZ=0 EndX=-62.677 EndY=-156.894 EndZ=0
  constraints (15):
    c: Tangent(g0,g3) = 1.5708
    c: Tangent(g0,g2) = -1.5708
    c: Tangent(g2,g1) = -1.5708
    c: Tangent(g3,g1) = 1.5708
    c: Vertical(g2)
    c: Coincident(g-4,g0)
    c: Coincident(g1,g-5)
    c: DistanceX(g-4,g0) = 1
    c: Tangent(g4,g7) = 1.5708
    c: Tangent(g4,g6) = -1.5708
    c: Tangent(g6,g5) = -1.5708
    c: Tangent(g7,g5) = 1.5708
    c: Coincident(g4,g0)
    c: Coincident(g1,g5)
    c: Coincident(g5,g-5)
FEATURE [PartDesign::Pocket] Pocket016
  BaseFeature = -> Pocket015
  Length = 2
  Length2 = 100
  Profile = -> Sketch027
  Type = 0
FEATURE [PartDesign::Pocket] Pocket017
  BaseFeature = -> Pocket016
  Length = 2
  Length2 = 100
  Profile = -> Sketch023
  Type = 0
FEATURE [PartDesign::Body] Body004  label="mould_male"
  Group = -> [ShapeBinder004,Sketch021,Pad006,Sketch022,Pad007,Sketch023,Sketch024,Pad008,DatumPlane003,Sketch025,Pocket014,DatumPlane004,Sketch026,Pocket015,DatumPlane005,Sketch027,Pocket016,Pocket017]
  Origin = -> Origin004
  Tip = -> Pocket017
FEATURE [PartDesign::Pocket] Pocket018
  BaseFeature = -> Pocket004
  Length = 0.1
  Length2 = 100
  Profile = -> Pocket004 [Face23]
  Type = 0
FEATURE [PartDesign::Pocket] Pocket019
  BaseFeature = -> Pocket018
  Length = 0.1
  Length2 = 100
  Profile = -> Pocket018 [Face31]
  Type = 0
FEATURE [PartDesign::Pocket] Pocket020
  BaseFeature = -> Pocket019
  Length = 0.1
  Length2 = 100
  Profile = -> Pocket019 [Face25]
  Type = 0
FEATURE [PartDesign::Pocket] Pocket021
  BaseFeature = -> Pocket020
  Length = 0.1
  Length2 = 100
  Profile = -> Pocket020 [Face30]
  Type = 0
FEATURE [PartDesign::Pocket] Pocket022
  BaseFeature = -> Pocket021
  Length = 0.1
  Length2 = 100
  Profile = -> Pocket021 [Face40]
  Type = 0
FEATURE [PartDesign::Pocket] Pocket023
  BaseFeature = -> Pocket022
  Length = 0.1
  Length2 = 100
  Profile = -> Pocket022 [Face43]
  Type = 0
FEATURE [Sketcher::SketchObject] Sketch028
  ExternalGeometry = -> [Pocket023]
  FullyConstrained = true
  MapMode = 5
  Placement = pos=(-6.10127,5e-16,46.4286) rot=(0,-1,0;0.130663rad)
  Support = -> [Pocket023]
  sketch-geometry (4):
    g0: ArcOfCircle CenterX=-50.3154 CenterY=182.684 CenterZ=0 NormalX=0 NormalY=0 NormalZ=1 AngleXU=0 Radius=5.075 StartAngle=1.5708 EndAngle=4.71239
    g1: ArcOfCircle CenterX=-45.3154 CenterY=182.684 CenterZ=0 NormalX=0 NormalY=0 NormalZ=1 AngleXU=0 Radius=5.075 StartAngle=4.71239 EndAngle=7.85398
    g2: LineSegment StartX=-50.3154 StartY=177.609 StartZ=0 EndX=-45.3154 EndY=177.609 EndZ=0
    g3: LineSegment StartX=-50.3154 StartY=187.759 StartZ=0 EndX=-45.3154 EndY=187.759 EndZ=0
  constraints (8):
    c: Tangent(g0,g3) = 1.5708
    c: Tangent(g0,g2) = -1.5708
    c: Tangent(g2,g1) = -1.5708
    c: Tangent(g3,g1) = 1.5708
    c: Horizontal(g2)
    c: Coincident(g-5,g0)
    c: Coincident(g-4,g1)
    c: DistanceY(g-5,g0) = 0.075
FEATURE [PartDesign::Pocket] Pocket024
  BaseFeature = -> Pocket023
  Length = 5
  Length2 = 100
  Profile = -> Sketch028
  Type = 1
FEATURE [Sketcher::SketchObject] Sketch029
  FullyConstrained = true
  MapMode = 5
  Support = -> [XY_Plane005]
  sketch-geometry (4):
    g0: LineSegment StartX=0 StartY=5.7 StartZ=0 EndX=12.6 EndY=5.7 EndZ=0
    g1: LineSegment StartX=12.6 StartY=5.7 StartZ=0 EndX=12.6 EndY=0 EndZ=0
    g2: LineSegment StartX=12.6 StartY=0 StartZ=0 EndX=0 EndY=0 EndZ=0
    g3: LineSegment StartX=0 StartY=0 StartZ=0 EndX=0 EndY=5.7 EndZ=0
  constraints (11):
    c: Coincident(g0,g1)
    c: Coincident(g1,g2)
    c: Coincident(g2,g3)
    c: Coincident(g3,g0)
    c: Horizontal(g0)
    c: Horizontal(g2)
    c: Vertical(g1)
    c: Vertical(g3)
    c: DistanceX(g2,g2) = 12.6
    c: DistanceY(g1,g1) = 5.7
    c: Coincident(g2,g-1)
FEATURE [PartDesign::Pad] Pad009
  Direction = (1,1,1)
  Length = 6.5
  Length2 = 100
  Profile = -> Sketch029
  Type = 0
FEATURE [Sketcher::SketchObject] Sketch030
  ExternalGeometry = -> [Pad009]
  FullyConstrained = true
  MapMode = 5
  Placement = pos=(0,5.7,0) rot=(0,0.707107,0.707107;3.14159rad)
  Support = -> [Pad009]
  sketch-geometry (4):
    g0: Circle CenterX=-9.55 CenterY=1.5 CenterZ=0 NormalX=0 NormalY=0 NormalZ=1 AngleXU=0 Radius=1
    g1: Circle CenterX=-3.05 CenterY=1.5 CenterZ=0 NormalX=0 NormalY=0 NormalZ=1 AngleXU=0 Radius=1
    g2: LineSegment StartX=-12.6 StartY=1.5 StartZ=0 EndX=0 EndY=1.5 EndZ=0
    g3: GeomPoint X=-6.3 Y=1.5 Z=0
  constraints (10):
    c: Horizontal(g0,g1)
    c: DistanceX(g0,g1) = 6.5
    c: Distance(g1,g-5) = 1.5
    c: PointOnObject(g2,g-3)
    c: PointOnObject(g2,g-4)
    c: Horizontal(g2)
    c: Symmetric(g2,g2,g3)
    c: Symmetric(g0,g1,g3)
    c: Equal(g1,g0)
    c: Diameter(g0) = 2
FEATURE [PartDesign::Pocket] Pocket025
  BaseFeature = -> Pad009
  Length = 5
  Length2 = 100
  Profile = -> Sketch030
  Type = 1
FEATURE [Sketcher::SketchObject] Sketch031
  ExternalGeometry = -> [Pocket025]
  FullyConstrained = true
  MapMode = 5
  Placement = pos=(0,5.7,0) rot=(0,0.707107,0.707107;3.14159rad)
  Support = -> [Pocket025]
  sketch-geometry (4):
    g0: LineSegment StartX=-11.6 StartY=6.5 StartZ=0 EndX=1.6 EndY=8 EndZ=0
    g1: LineSegment StartX=-10.7143 StartY=6.5 StartZ=0 EndX=1.61129 EndY=7.90064 EndZ=0
    g2: LineSegment StartX=1.61129 StartY=7.90064 StartZ=0 EndX=1.6 EndY=8 EndZ=0
    g3: LineSegment StartX=-11.6 StartY=6.5 StartZ=0 EndX=-10.7143 EndY=6.5 EndZ=0
  constraints (12):
    c: PointOnObject(g0,g-3)
    c: DistanceX(g-3,g0) = 1
    c: DistanceX(g-3,g0) = 14.2
    c: DistanceY(g-1,g0) = 8
    c: PointOnObject(g1,g-3)
    c: Parallel(g1,g0)
    c: Coincident(g2,g1)
    c: Coincident(g2,g0)
    c: Perpendicular(g1,g2)
    c: Distance(g2) = 0.1
    c: Coincident(g3,g0)
    c: Coincident(g3,g1)
FEATURE [PartDesign::Pad] Pad010
  BaseFeature = -> Pocket025
  Direction = (1,1,1)
  Length = 5.7
  Length2 = 100
  Profile = -> Sketch031
  Reversed = true
  Type = 0
FEATURE [PartDesign::Body] Body005  label="switch"
  Group = -> [Sketch029,Pad009,Sketch030,Pocket025,Sketch031,Pad010]
  Origin = -> Origin005
  Tip = -> Pad010
FEATURE [Mesh::Feature] leg_redesigned_switch  label="leg_redesigned-switch"
  Placement = pos=(-53.3437,168.056,56.936) rot=(-0.639179,0.541013,0.546586;1.99756rad)
FEATURE [PartDesign::Pad] Pad011
  BaseFeature = -> Pocket024
  Direction = (1,1,1)
  Length = 8.6
  Length2 = 100
  Profile = -> Pocket024 [Face46]
  Type = 0
FEATURE [Sketcher::SketchObject] Sketch032
  ExternalGeometry = -> [Pad011]
  FullyConstrained = true
  MapMode = 5
  Placement = pos=(-44.9291,0,-5.90422) rot=(0.550513,0.550513,0.627591;2.02067rad)
  Support = -> [Pad011]
  sketch-geometry (10):
    g0: LineSegment StartX=169.684 StartY=59.4278 StartZ=0 EndX=169.684 EndY=46.8278 EndZ=0
    g1: GeomPoint X=169.684 Y=53.1278 Z=0
    g2: ArcOfCircle CenterX=169.684 CenterY=56.3778 CenterZ=0 NormalX=0 NormalY=0 NormalZ=1 AngleXU=0 Radius=1.1 StartAngle=1.5708 EndAngle=4.71239
    g3: ArcOfCircle CenterX=171.684 CenterY=56.3778 CenterZ=0 NormalX=0 NormalY=0 NormalZ=1 AngleXU=0 Radius=1.1 StartAngle=4.71239 EndAngle=7.85398
    g4: LineSegment StartX=169.684 StartY=55.2778 StartZ=0 EndX=171.684 EndY=55.2778 EndZ=0
    g5: LineSegment StartX=169.684 StartY=57.4778 StartZ=0 EndX=171.684 EndY=57.4778 EndZ=0
    g6: ArcOfCircle CenterX=169.684 CenterY=49.8778 CenterZ=0 NormalX=0 NormalY=0 NormalZ=1 AngleXU=0 Radius=1.1 StartAngle=1.5708 EndAngle=4.71239
    g7: ArcOfCircle CenterX=171.684 CenterY=49.8778 CenterZ=0 NormalX=0 NormalY=0 NormalZ=1 AngleXU=0 Radius=1.1 StartAngle=4.71239 EndAngle=7.85398
    g8: LineSegment StartX=169.684 StartY=48.7778 StartZ=0 EndX=171.684 EndY=48.7778 EndZ=0
    g9: LineSegment StartX=169.684 StartY=50.9778 StartZ=0 EndX=171.684 EndY=50.9778 EndZ=0
  constraints (25):
    c: PointOnObject(g0,g-4)
    c: Vertical(g0)
    c: Horizontal(g0,g-5)
    c: Symmetric(g0,g0,g1)
    c: Tangent(g2,g5) = 1.5708
    c: Tangent(g2,g4) = -1.5708
    c: Tangent(g4,g3) = -1.5708
    c: Tangent(g5,g3) = 1.5708
    c: Horizontal(g4)
    c: Equal(g2,g3)
    c: PointOnObject(g2,g0)
    c: Tangent(g6,g9) = 1.5708
    c: Tangent(g6,g8) = -1.5708
    c: Tangent(g8,g7) = -1.5708
    c: Tangent(g9,g7) = 1.5708
    c: Horizontal(g8)
    c: Equal(g6,g7)
    c: DistanceX(g0,g-4) = 5
    c: PointOnObject(g6,g0)
    c: DistanceY(g6,g2) = 6.5
    c: Diameter(g3) = 2.2
    c: Equal(g7,g3)
    c: Equal(g9,g4)
    c: DistanceX(g5,g5) = 2
    c: DistanceY(g2,g0) = 3.05
FEATURE [PartDesign::Fillet] Fillet002
  Base = -> Pocket008
  BaseFeature = -> Pocket008
  Radius = 2.5
  SupportTransform = false
FEATURE [PartDesign::Fillet] Fillet003
  Base = -> Fillet002 [Edge127,Edge125,Edge130,Edge129]
  BaseFeature = -> Fillet002
  Radius = 4
  SupportTransform = false
FEATURE [PartDesign::Plane] DatumPlane
  AttachmentOffset = pos=(0,0,-5) rot=(0,0,1;0rad)
  Length = 126.593
  MapMode = 5
  Placement = pos=(-1.54106,-1.2e-15,11.727) rot=(0.997867,0,0.065285;3.14159rad)
  ResizeMode = 0
  Support = -> [Fillet003]
  Width = 244.698
FEATURE [Sketcher::SketchObject] Sketch034
  ExternalGeometry = -> [Fillet003]
  FullyConstrained = true
  MapMode = 5
  Placement = pos=(-1.54106,-1.2e-15,11.727) rot=(0.997867,0,0.065285;3.14159rad)
  Support = -> [DatumPlane]
  sketch-geometry (8):
    g0: ArcOfCircle CenterX=-50.3154 CenterY=-182.684 CenterZ=0 NormalX=0 NormalY=0 NormalZ=1 AngleXU=0 Radius=5 StartAngle=1.5708 EndAngle=4.71239
    g1: ArcOfCircle CenterX=-45.3154 CenterY=-182.684 CenterZ=0 NormalX=0 NormalY=0 NormalZ=1 AngleXU=0 Radius=5 StartAngle=4.71239 EndAngle=7.85398
    g2: LineSegment StartX=-50.3154 StartY=-187.684 StartZ=0 EndX=-45.3154 EndY=-187.684 EndZ=0
    g3: LineSegment StartX=-50.3154 StartY=-177.684 StartZ=0 EndX=-45.3154 EndY=-177.684 EndZ=0
    g4: ArcOfCircle CenterX=-50.3154 CenterY=-182.684 CenterZ=0 NormalX=0 NormalY=0 NormalZ=1 AngleXU=0 Radius=4 StartAngle=1.5708 EndAngle=4.71239
    g5: ArcOfCircle CenterX=-45.3154 CenterY=-182.684 CenterZ=0 NormalX=0 NormalY=0 NormalZ=1 AngleXU=0 Radius=4 StartAngle=4.71239 EndAngle=7.85398
    g6: LineSegment StartX=-50.3154 StartY=-186.684 StartZ=0 EndX=-45.3154 EndY=-186.684 EndZ=0
    g7: LineSegment StartX=-50.3154 StartY=-178.684 StartZ=0 EndX=-45.3154 EndY=-178.684 EndZ=0
  constraints (15):
    c: Tangent(g0,g3) = 1.5708
    c: Tangent(g0,g2) = -1.5708
    c: Tangent(g2,g1) = -1.5708
    c: Tangent(g3,g1) = 1.5708
    c: Coincident(g0,g-3)
    c: Coincident(g-5,g1)
    c: Coincident(g-4,g0)
    c: Tangent(g4,g7) = 1.5708
    c: Tangent(g4,g6) = -1.5708
    c: Tangent(g6,g5) = -1.5708
    c: Tangent(g7,g5) = 1.5708
    c: Horizontal(g6)
    c: Coincident(g0,g4)
    c: Coincident(g5,g1)
    c: DistanceY(g4,g0) = 1
FEATURE [PartDesign::Pocket] Pocket027
  BaseFeature = -> Fillet003
  Length = 1
  Length2 = 100
  Profile = -> Sketch034
  Type = 0
FEATURE [PartDesign::Plane] DatumPlane006
  AttachmentOffset = pos=(0,0,-7) rot=(0,0,1;0rad)
  Length = 126.593
  MapMode = 5
  Placement = pos=(-1.80165,-1.4e-15,13.7099) rot=(0.997867,0,0.065285;3.14159rad)
  ResizeMode = 0
  Support = -> [Pocket027]
  Width = 244.698
FEATURE [Sketcher::SketchObject] Sketch035
  ExternalGeometry = -> [Pocket027]
  FullyConstrained = true
  MapMode = 5
  Placement = pos=(-1.80165,-1.4e-15,13.7099) rot=(0.997867,0,0.065285;3.14159rad)
  Support = -> [DatumPlane006]
  sketch-geometry (8):
    g0: ArcOfCircle CenterX=-50.3154 CenterY=-182.684 CenterZ=0 NormalX=0 NormalY=0 NormalZ=1 AngleXU=0 Radius=5 StartAngle=1.5708 EndAngle=4.71239
    g1: ArcOfCircle CenterX=-45.3154 CenterY=-182.684 CenterZ=0 NormalX=0 NormalY=0 NormalZ=1 AngleXU=0 Radius=5 StartAngle=4.71239 EndAngle=7.85398
    g2: LineSegment StartX=-50.3154 StartY=-187.684 StartZ=0 EndX=-45.3154 EndY=-187.684 EndZ=0
    g3: LineSegment StartX=-50.3154 StartY=-177.684 StartZ=0 EndX=-45.3154 EndY=-177.684 EndZ=0
    g4: ArcOfCircle CenterX=-50.3154 CenterY=-182.684 CenterZ=0 NormalX=0 NormalY=0 NormalZ=1 AngleXU=0 Radius=4 StartAngle=1.5708 EndAngle=4.71239
    g5: ArcOfCircle CenterX=-45.3154 CenterY=-182.684 CenterZ=0 NormalX=0 NormalY=0 NormalZ=1 AngleXU=0 Radius=4 StartAngle=4.71239 EndAngle=7.85398
    g6: LineSegment StartX=-50.3154 StartY=-186.684 StartZ=0 EndX=-45.3154 EndY=-186.684 EndZ=0
    g7: LineSegment StartX=-50.3154 StartY=-178.684 StartZ=0 EndX=-45.3154 EndY=-178.684 EndZ=0
  constraints (16):
    c: Tangent(g0,g3) = 1.5708
    c: Tangent(g0,g2) = -1.5708
    c: Tangent(g2,g1) = -1.5708
    c: Tangent(g3,g1) = 1.5708
    c: Horizontal(g2)
    c: Equal(g0,g1)
    c: Coincident(g-3,g0)
    c: Coincident(g1,g-5)
    c: Tangent(g4,g7) = 1.5708
    c: Tangent(g4,g6) = -1.5708
    c: Tangent(g6,g5) = -1.5708
    c: Tangent(g7,g5) = 1.5708
    c: Horizontal(g6)
    c: Coincident(g4,g0)
    c: Coincident(g5,g1)
    c: DistanceY(g4,g0) = 1
FEATURE [PartDesign::Pocket] Pocket028
  BaseFeature = -> Pocket027
  Length = 1
  Length2 = 100
  Profile = -> Sketch035
  Type = 0
FEATURE [PartDesign::Chamfer] Chamfer001
  Angle = 45
  Base = -> Pocket028 [Edge17,Edge3,Edge19,Edge20]
  BaseFeature = -> Pocket028
  ChamferType = 0
  FlipDirection = false
  Size = 0.95
  Size2 = 1
  SupportTransform = false
FEATURE [PartDesign::Chamfer] Chamfer002
  Angle = 45
  Base = -> Chamfer001 [Edge83,Edge82,Edge81,Edge84]
  BaseFeature = -> Chamfer001
  ChamferType = 0
  FlipDirection = false
  Size = 0.95
  Size2 = 1
  SupportTransform = false
FEATURE [PartDesign::Chamfer] Chamfer003
  Angle = 45
  Base = -> Chamfer002 [Edge26,Edge28,Edge32,Edge30]
  BaseFeature = -> Chamfer002
  ChamferType = 0
  FlipDirection = false
  Size = 0.45
  Size2 = 1
  SupportTransform = false
FEATURE [PartDesign::Chamfer] Chamfer004
  Angle = 45
  Base = -> Chamfer003 [Edge55,Edge54,Edge53,Edge56]
  BaseFeature = -> Chamfer003
  ChamferType = 0
  FlipDirection = false
  Size = 0.95
  Size2 = 1
  SupportTransform = false
FEATURE [Sketcher::SketchObject] Sketch036
  ExternalGeometry = -> [Chamfer004]
  FullyConstrained = true
  MapMode = 5
  Placement = pos=(-6.36185,-4.4e-15,48.4116) rot=(0,-1,0;0.130663rad)
  Support = -> [Chamfer004]
  sketch-geometry (4):
    g0: LineSegment StartX=-50.9654 StartY=176.134 StartZ=0 EndX=-50.9654 EndY=178.684 EndZ=0
    g1: LineSegment StartX=-50.9654 StartY=176.134 StartZ=0 EndX=-54.9654 EndY=176.134 EndZ=0
    g2: LineSegment StartX=-54.9654 StartY=176.134 StartZ=0 EndX=-53.9654 EndY=178.684 EndZ=0
    g3: LineSegment StartX=-53.9654 StartY=178.684 StartZ=0 EndX=-50.9654 EndY=178.684 EndZ=0
  constraints (11):
    c: Coincident(g0,g-3)
    c: PointOnObject(g0,g-4)
    c: Perpendicular(g0,g-4)
    c: Coincident(g1,g0)
    c: Horizontal(g1)
    c: Coincident(g2,g-6)
    c: Vertical(g1,g-6)
    c: Coincident(g2,g1)
    c: Coincident(g3,g2)
    c: PointOnObject(g3,g0)
    c: Horizontal(g3)
FEATURE [PartDesign::Pad] Pad012
  BaseFeature = -> Chamfer004
  Direction = (1,1,1)
  Length = 8
  Length2 = 100
  Profile = -> Sketch036
  Type = 0
FEATURE [PartDesign::Pad] Pad013
  BaseFeature = -> Pad012
  Direction = (1,1,1)
  Length = 2
  Length2 = 100
  Profile = -> Pad012 [Face57]
  Type = 0
FEATURE [PartDesign::Fillet] Fillet
  Base = -> Pad013 [Edge159]
  BaseFeature = -> Pad013
  Radius = 0.5
  SupportTransform = false
FEATURE [PartDesign::Pocket] Pocket029
  BaseFeature = -> Pad011
  Length = 4
  Length2 = 100
  Profile = -> Sketch032
  Type = 1
FEATURE [Sketcher::SketchObject] Sketch037
  ExternalGeometry = -> [Fillet]
  FullyConstrained = true
  MapMode = 5
  Placement = pos=(-6.36185,-4.4e-15,48.4116) rot=(0,-1,0;0.130663rad)
  Support = -> [Fillet]
  sketch-geometry (5):
    g0: LineSegment StartX=-44.6654 StartY=178.684 StartZ=0 EndX=-41.6654 EndY=178.684 EndZ=0
    g1: LineSegment StartX=-41.6654 StartY=178.684 StartZ=0 EndX=-40.6654 EndY=176.134 EndZ=0
    g2: LineSegment StartX=-40.6654 StartY=176.134 StartZ=0 EndX=-44.6654 EndY=176.134 EndZ=0
    g3: LineSegment StartX=-44.6654 StartY=176.134 StartZ=0 EndX=-44.6654 EndY=178.684 EndZ=0
    g4: LineSegment StartX=-44.6654 StartY=178.684 StartZ=0 EndX=-41.6654 EndY=178.684 EndZ=0
  constraints (10):
    c: Coincident(g0,g-3)
    c: Coincident(g0,g-7)
    c: Coincident(g1,g0)
    c: Coincident(g1,g-6)
    c: Coincident(g2,g1)
    c: Coincident(g2,g-4)
    c: Coincident(g3,g2)
    c: Coincident(g3,g0)
    c: Coincident(g4,g0)
    c: Coincident(g4,g0)
FEATURE [PartDesign::Pocket] Pocket030
  BaseFeature = -> Fillet
  Length = 7
  Length2 = 100
  Profile = -> Sketch037
  Reversed = true
  Type = 1
FEATURE [Sketcher::SketchObject] Sketch038
  ExternalGeometry = -> [Pocket030]
  FullyConstrained = true
  MapMode = 5
  Placement = pos=(-6.36185,-4.4e-15,48.4116) rot=(0,-1,0;0.130663rad)
  Support = -> [Pocket030]
  sketch-geometry (3):
    g0: LineSegment StartX=-42.4867 StartY=176.134 StartZ=0 EndX=-41.1784 EndY=177.442 EndZ=0
    g1: LineSegment StartX=-42.4867 StartY=176.134 StartZ=0 EndX=-40.6654 EndY=176.134 EndZ=0
    g2: LineSegment StartX=-40.6654 StartY=176.134 StartZ=0 EndX=-41.1784 EndY=177.442 EndZ=0
  constraints (6):
    c: Coincident(g0,g-3)
    c: Coincident(g0,g-4)
    c: Coincident(g1,g0)
    c: Coincident(g1,g-6)
    c: Coincident(g2,g1)
    c: Coincident(g2,g0)
FEATURE [PartDesign::Pocket] Pocket031
  BaseFeature = -> Pocket030
  Length = 2
  Length2 = 100
  Profile = -> Sketch038
  Type = 0
FEATURE [PartDesign::Body] Body  label="Slider"
  Group = -> [ShapeBinder003,Sketch009,Pad002,Sketch010,Pad003,Sketch011,Pad004,Sketch012,Pocket005,Sketch013,Pocket006,Sketch014,Pocket007,Sketch015,Pocket008,Fillet002,Fillet003,DatumPlane,Sketch034,Pocket027,DatumPlane006,Sketch035,Pocket028,Chamfer001,Chamfer002,Chamfer003,Chamfer004,Sketch036,Pad012,Pad013,Fillet,Sketch037,Pocket030,Sketch038,Pocket031]
  Origin = -> Origin
  Tip = -> Pocket031
FEATURE [Sketcher::SketchObject] Sketch039
  FullyConstrained = false
  MapMode = 5
  Placement = pos=(0,166.684,0) rot=(0,0.707107,0.707107;3.14159rad)
  sketch-geometry (4):
    g0: LineSegment StartX=57.6635 StartY=52.1255 StartZ=0 EndX=56.0544 EndY=39.8812 EndZ=0
    g1: LineSegment StartX=56.0544 StartY=39.8812 StartZ=0 EndX=60.0544 EndY=39.3555 EndZ=0
    g2: LineSegment StartX=60.0544 StartY=39.3555 StartZ=0 EndX=61.6635 EndY=51.5998 EndZ=0
    g3: LineSegment StartX=61.6635 StartY=51.5998 StartZ=0 EndX=57.6635 EndY=52.1255 EndZ=0
  constraints (8):
    c: Coincident(g1,g0)
    c: Coincident(g3,g0)
    c: Coincident(g2,g3)
    c: Perpendicular(g3,g2)
    c: Perpendicular(g1,g0)
    c: Coincident(g2,g1)
    c: Parallel(g2,g0)
    c: DistanceX(g3,g3) = 4
FEATURE [Part::Feature] Component004002  label="left_part_original_shape001"
  shape: bbox 45.1 x 3 x 112.7 mm, 1032 faces, 0 solids (baked)
FEATURE [PartDesign::FeatureBase] BaseFeature
  BaseFeature = -> Component004002
FEATURE [Sketcher::SketchObject] Sketch040
  ExternalGeometry = -> [BaseFeature]
  FullyConstrained = true
  MapMode = 5
  Placement = pos=(0,166.684,0) rot=(0,0.707107,0.707107;3.14159rad)
  Support = -> [BaseFeature]
  sketch-geometry (35):
    g0: LineSegment StartX=54.0461 StartY=19.2636 StartZ=0 EndX=90.2154 EndY=91.7231 EndZ=0
    g1: LineSegment StartX=90.2154 StartY=91.7231 StartZ=0 EndX=81.5091 EndY=125.623 EndZ=0
    g2: LineSegment StartX=81.5091 StartY=125.623 StartZ=0 EndX=74.1673 EndY=131.915 EndZ=0
    g3: LineSegment StartX=74.1673 StartY=131.915 StartZ=0 EndX=71.3472 EndY=131.698 EndZ=0
    g4: LineSegment StartX=71.3472 StartY=131.698 StartZ=0 EndX=67.5413 EndY=127.257 EndZ=0
    g5: LineSegment StartX=67.5413 StartY=127.257 StartZ=0 EndX=71.1705 EndY=124.146 EndZ=0
    g6: LineSegment StartX=71.1705 StartY=124.146 StartZ=0 EndX=58.1559 EndY=108.96 EndZ=0
    g7: LineSegment StartX=58.1559 StartY=108.96 StartZ=0 EndX=54.5268 EndY=112.07 EndZ=0
    g8: LineSegment StartX=54.5268 StartY=112.07 StartZ=0 EndX=50.6605 EndY=107.559 EndZ=0
    g9: LineSegment StartX=50.6605 StartY=107.559 StartZ=0 EndX=54.3918 EndY=93.0306 EndZ=0
    g10: LineSegment StartX=54.3918 StartY=93.0306 StartZ=0 EndX=48.5652 EndY=48.7015 EndZ=0
    g11: LineSegment StartX=48.5652 StartY=48.7015 StartZ=0 EndX=45.116 EndY=22.4543 EndZ=0
    g12: LineSegment StartX=46.8384 StartY=20.2108 StartZ=0 EndX=54.0461 EndY=19.2636 EndZ=0
    g13: LineSegment StartX=45.116 StartY=22.4543 StartZ=0 EndX=46.8384 EndY=20.2108 EndZ=0
    g14: LineSegment StartX=61.9811 StartY=97.2566 StartZ=0 EndX=77.051 EndY=114.841 EndZ=0
    g15: LineSegment StartX=77.051 StartY=114.841 StartZ=0 EndX=81.7524 EndY=96.535 EndZ=0
    g16: LineSegment StartX=81.7524 StartY=96.535 StartZ=0 EndX=61.9811 EndY=97.2566 EndZ=0
    g17: LineSegment StartX=60.8292 StartY=88.2926 StartZ=0 EndX=80.3242 EndY=87.5811 EndZ=0
    g18: LineSegment StartX=80.3242 StartY=87.5811 StartZ=0 EndX=61.2023 EndY=49.2734 EndZ=0
    g19: LineSegment StartX=61.2023 StartY=49.2734 StartZ=0 EndX=55.794 EndY=49.9843 EndZ=0
    g20: LineSegment StartX=55.794 StartY=49.9843 StartZ=0 EndX=60.8292 EndY=88.2926 EndZ=0
    g21: LineSegment StartX=51.5367 StartY=44.4923 StartZ=0 EndX=56.5734 EndY=43.8304 EndZ=0
    g22: LineSegment StartX=56.5734 StartY=43.8304 StartZ=0 EndX=55.7916 EndY=37.8815 EndZ=0
    g23: LineSegment StartX=55.7916 StartY=37.8815 StartZ=0 EndX=50.7549 EndY=38.5434 EndZ=0
    g24: LineSegment StartX=50.7549 StartY=38.5434 StartZ=0 EndX=51.5367 EndY=44.4923 EndZ=0
    g25: LineSegment StartX=49.988 StartY=32.5926 StartZ=0 EndX=54.995 EndY=31.9346 EndZ=0
    g26: LineSegment StartX=54.995 StartY=31.9346 StartZ=0 EndX=54.2133 EndY=25.9858 EndZ=0
    g27: LineSegment StartX=54.2133 StartY=25.9858 StartZ=0 EndX=49.2063 EndY=26.6437 EndZ=0
    g28: LineSegment StartX=49.2063 StartY=26.6437 StartZ=0 EndX=49.988 EndY=32.5926 EndZ=0
    g29: Circle CenterX=52.8473 CenterY=35.2426 CenterZ=0 NormalX=0 NormalY=0 NormalZ=1 AngleXU=0 Radius=1.5
    g30: Circle CenterX=84.9275 CenterY=91.9161 CenterZ=0 NormalX=0 NormalY=0 NormalZ=1 AngleXU=0 Radius=1.55
    g31: Circle CenterX=54.5651 CenterY=107.428 CenterZ=0 NormalX=0 NormalY=0 NormalZ=1 AngleXU=0 Radius=1.05
    g32: Circle CenterX=62.1305 CenterY=108.188 CenterZ=0 NormalX=0 NormalY=0 NormalZ=1 AngleXU=0 Radius=1.05
    g33: Circle CenterX=72.5421 CenterY=120.337 CenterZ=0 NormalX=0 NormalY=0 NormalZ=1 AngleXU=0 Radius=1.05
    g34: Circle CenterX=72.1347 CenterY=127.93 CenterZ=0 NormalX=0 NormalY=0 NormalZ=1 AngleXU=0 Radius=1.05
  constraints (76):
    c: Coincident(g0,g-6)
    c: Coincident(g0,g-23)
    c: Coincident(g1,g0)
    c: Coincident(g1,g-33)
    c: Coincident(g2,g1)
    c: Coincident(g2,g-33)
    c: Coincident(g3,g2)
    c: Coincident(g3,g-32)
    c: Coincident(g4,g3)
    c: Coincident(g4,g-30)
    c: Coincident(g5,g4)
    c: Coincident(g5,g-28)
    c: Coincident(g6,g-27)
    c: Coincident(g7,g-31)
    c: Coincident(g8,g-31)
    c: Coincident(g7,g6)
    c: Coincident(g5,g6)
    c: Coincident(g7,g8)
    c: Coincident(g9,g8)
    c: Coincident(g9,g-22)
    c: Coincident(g10,g9)
    c: Coincident(g10,g-17)
    c: Coincident(g11,g10)
    c: Coincident(g11,g-5)
    c: Coincident(g12,g-4)
    c: Coincident(g12,g0)
    c: Coincident(g13,g11)
    c: Coincident(g13,g12)
    c: Coincident(g14,g-25)
    c: Coincident(g14,g-25)
    c: Coincident(g15,g14)
    c: Coincident(g15,g-24)
    c: Coincident(g16,g15)
    c: Coincident(g16,g14)
    c: Coincident(g17,g-20)
    c: Coincident(g17,g-19)
    c: Coincident(g18,g17)
    c: Coincident(g18,g-18)
    c: Coincident(g19,g18)
    c: Coincident(g19,g-20)
    c: Coincident(g20,g19)
    c: Coincident(g20,g17)
    c: Coincident(g21,g-15)
    c: Coincident(g21,g-16)
    c: Coincident(g22,g21)
    c: Coincident(g22,g-16)
    c: Coincident(g23,g22)
    c: Coincident(g23,g-15)
    c: Coincident(g24,g21)
    c: Coincident(g24,g23)
    c: Coincident(g25,g-9)
    c: Coincident(g25,g-10)
    c: Coincident(g26,g25)
    c: Coincident(g26,g-10)
    c: Coincident(g27,g26)
    c: Coincident(g27,g-8)
    c: Coincident(g28,g27)
    c: Coincident(g28,g25)
    c: PointOnObject(g-11,g29)
    c: PointOnObject(g-12,g29)
    c: PointOnObject(g-13,g29)
    c: PointOnObject(g-43,g30)
    c: PointOnObject(g-44,g30)
    c: PointOnObject(g-42,g30)
    c: PointOnObject(g-40,g31)
    c: PointOnObject(g-40,g31)
    c: PointOnObject(g-41,g31)
    c: PointOnObject(g-38,g32)
    c: PointOnObject(g-39,g32)
    c: PointOnObject(g-39,g32)
    c: PointOnObject(g-36,g33)
    c: PointOnObject(g-37,g33)
    c: PointOnObject(g-45,g33)
    c: PointOnObject(g-35,g34)
    c: PointOnObject(g-35,g34)
    c: PointOnObject(g-34,g34)
FEATURE [PartDesign::Pad] Pad014
  BaseFeature = -> BaseFeature
  Direction = (1,1,1)
  Length = 3
  Length2 = 100
  Profile = -> Sketch040
  Reversed = true
  Type = 0
FEATURE [PartDesign::Pocket] Pocket032
  BaseFeature = -> Pad014
  Length = 1.5
  Length2 = 100
  Profile = -> Sketch039
  Type = 0
FEATURE [PartDesign::Body] Body006  label="left_body"
  BaseFeature = -> Component004002
  Group = -> [BaseFeature,Sketch039,Sketch040,Pad014,Pocket032]
  Origin = -> Origin006
  Tip = -> Pocket032
FEATURE [Sketcher::SketchObject] Sketch041
  ExternalGeometry = -> [Pocket029]
  FullyConstrained = true
  MapMode = 5
  Placement = pos=(-6.10127,5e-16,46.4286) rot=(0,-1,0;0.130663rad)
  Support = -> [Pocket029]
  sketch-geometry (4):
    g0: ArcOfCircle CenterX=-50.3154 CenterY=182.684 CenterZ=0 NormalX=0 NormalY=0 NormalZ=1 AngleXU=0 Radius=5.075 StartAngle=1.5708 EndAngle=4.71239
    g1: ArcOfCircle CenterX=-45.3154 CenterY=182.684 CenterZ=0 NormalX=0 NormalY=0 NormalZ=1 AngleXU=0 Radius=5.075 StartAngle=4.71239 EndAngle=7.85398
    g2: LineSegment StartX=-50.3154 StartY=177.609 StartZ=0 EndX=-45.3154 EndY=177.609 EndZ=0
    g3: LineSegment StartX=-50.3154 StartY=187.759 StartZ=0 EndX=-45.3154 EndY=187.759 EndZ=0
  constraints (8):
    c: Tangent(g0,g3) = 1.5708
    c: Tangent(g0,g2) = -1.5708
    c: Tangent(g2,g1) = -1.5708
    c: Tangent(g3,g1) = 1.5708
    c: Horizontal(g2)
    c: Coincident(g0,g-4)
    c: Coincident(g1,g-6)
    c: DistanceY(g-4,g0) = 0.025
FEATURE [PartDesign::Pocket] Pocket033
  BaseFeature = -> Pocket029
  Length = 5
  Length2 = 100
  Profile = -> Sketch041
  Type = 1
FEATURE [PartDesign::Body] Body001  label="mid_piece"
  Group = -> [ShapeBinder,Sketch,ShapeBinder001,ShapeBinder002,Pad,Sketch002,Pad001,Sketch003,Pocket,Sketch004,Pocket001,Sketch005,Pocket002,Sketch006,Pocket003,Chamfer,Sketch008,Pocket004,Pocket018,Pocket019,Pocket020,Pocket021,Pocket022,Pocket023,Sketch028,Pocket024,Pad011,Sketch032,Pocket029,Sketch041,Pocket033]
  Origin = -> Origin001
  Tip = -> Pocket033
FEATURE [PartDesign::ShapeBinder] ShapeBinder005
  Placement = pos=(5.21167,0,-39.659) rot=(0,0,1;0rad)
  Support = -> [Pocket031]
  TraceSupport = false
FEATURE [Sketcher::SketchObject] Sketch042
  ExternalGeometry = -> [ShapeBinder005]
  FullyConstrained = true
  MapMode = 5
  Placement = pos=(-0.889605,-4.7e-15,6.76959) rot=(0.997867,0,0.065285;3.14159rad)
  Support = -> [ShapeBinder005]
  sketch-geometry (4):
    g0: ArcOfCircle CenterX=-50.3154 CenterY=-182.684 CenterZ=0 NormalX=0 NormalY=0 NormalZ=1 AngleXU=0 Radius=7 StartAngle=1.5708 EndAngle=4.71239
    g1: ArcOfCircle CenterX=-45.3154 CenterY=-182.684 CenterZ=0 NormalX=0 NormalY=0 NormalZ=1 AngleXU=0 Radius=7 StartAngle=4.71239 EndAngle=7.85398
    g2: LineSegment StartX=-50.3154 StartY=-189.684 StartZ=0 EndX=-45.3154 EndY=-189.684 EndZ=0
    g3: LineSegment StartX=-50.3154 StartY=-175.684 StartZ=0 EndX=-45.3154 EndY=-175.684 EndZ=0
  constraints (8):
    c: Tangent(g0,g3) = 1.5708
    c: Tangent(g0,g2) = -1.5708
    c: Tangent(g2,g1) = -1.5708
    c: Tangent(g3,g1) = 1.5708
    c: Horizontal(g2)
    c: Coincident(g1,g-6)
    c: Coincident(g0,g-5)
    c: DistanceY(g0,g0) = 7
FEATURE [PartDesign::Pad] Pad015
  Direction = (1,1,1)
  Length = 11
  Length2 = 100
  Placement = pos=(5.21167,0,-39.659) rot=(0,0,1;0rad)
  Profile = -> Sketch042
  Reversed = true
  Type = 0
FEATURE [PartDesign::Pad] Pad016
  BaseFeature = -> Pad015
  Direction = (1,1,1)
  Length = 2
  Length2 = 100
  Placement = pos=(5.21167,0,-39.659) rot=(0,0,1;0rad)
  Profile = -> Pad015 [Face5]
  Type = 0
FEATURE [PartDesign::Fillet] Fillet004
  Base = -> Pad016 [Edge13,Edge17,Edge20,Edge19]
  BaseFeature = -> Pad016
  Placement = pos=(5.21167,0,-39.659) rot=(0,0,1;0rad)
  Radius = 4
  SupportTransform = false
FEATURE [PartDesign::Chamfer] Chamfer005
  Angle = 45
  Base = -> Fillet004 [Edge3,Edge6,Edge12,Edge11]
  BaseFeature = -> Fillet004
  ChamferType = 0
  FlipDirection = false
  Placement = pos=(5.21167,0,-39.659) rot=(0,0,1;0rad)
  Size = 1
  Size2 = 1
  SupportTransform = false
FEATURE [Sketcher::SketchObject] Sketch043
  ExternalGeometry = -> [Chamfer005]
  FullyConstrained = true
  MapMode = 5
  Placement = pos=(-2.32281,-7.3e-15,17.6758) rot=(0,-1,0;0.130663rad)
  Support = -> [Chamfer005]
  sketch-geometry (4):
    g0: ArcOfCircle CenterX=-50.3154 CenterY=182.684 CenterZ=0 NormalX=0 NormalY=0 NormalZ=1 AngleXU=0 Radius=5 StartAngle=1.5708 EndAngle=4.71239
    g1: ArcOfCircle CenterX=-45.3154 CenterY=182.684 CenterZ=0 NormalX=0 NormalY=0 NormalZ=1 AngleXU=0 Radius=5 StartAngle=4.71239 EndAngle=7.85398
    g2: LineSegment StartX=-50.3154 StartY=177.684 StartZ=0 EndX=-45.3154 EndY=177.684 EndZ=0
    g3: LineSegment StartX=-50.3154 StartY=187.684 StartZ=0 EndX=-45.3154 EndY=187.684 EndZ=0
  constraints (8):
    c: Tangent(g0,g3) = 1.5708
    c: Tangent(g0,g2) = -1.5708
    c: Tangent(g2,g1) = -1.5708
    c: Tangent(g3,g1) = 1.5708
    c: Horizontal(g2)
    c: Coincident(g0,g-3)
    c: Coincident(g1,g-4)
    c: DistanceY(g0,g0) = 5
FEATURE [PartDesign::Pocket] Pocket034
  BaseFeature = -> Chamfer005
  Length = 11
  Length2 = 100
  Placement = pos=(5.21167,0,-39.659) rot=(0,0,1;0rad)
  Profile = -> Sketch043
  Type = 0
FEATURE [PartDesign::Plane] DatumPlane007
  AttachmentOffset = pos=(0,0,5) rot=(0,0,1;0rad)
  Length = 117.546
  MapMode = 5
  Placement = pos=(-1.54106,-1.06e-14,11.727) rot=(0,-1,0;0.130663rad)
  ResizeMode = 0
  Support = -> [Pocket034]
  Width = 242.45
FEATURE [Sketcher::SketchObject] Sketch044
  ExternalGeometry = -> [Pocket034]
  FullyConstrained = true
  MapMode = 5
  Placement = pos=(-1.54106,-1.06e-14,11.727) rot=(0,-1,0;0.130663rad)
  Support = -> [DatumPlane007]
  sketch-geometry (8):
    g0: ArcOfCircle CenterX=-50.3154 CenterY=182.684 CenterZ=0 NormalX=0 NormalY=0 NormalZ=1 AngleXU=0 Radius=5 StartAngle=1.5708 EndAngle=4.71239
    g1: ArcOfCircle CenterX=-45.3154 CenterY=182.684 CenterZ=0 NormalX=0 NormalY=0 NormalZ=1 AngleXU=0 Radius=5 StartAngle=4.71239 EndAngle=7.85398
    g2: LineSegment StartX=-50.3154 StartY=177.684 StartZ=0 EndX=-45.3154 EndY=177.684 EndZ=0
    g3: LineSegment StartX=-50.3154 StartY=187.684 StartZ=0 EndX=-45.3154 EndY=187.684 EndZ=0
    g4: ArcOfCircle CenterX=-50.3154 CenterY=182.684 CenterZ=0 NormalX=0 NormalY=0 NormalZ=1 AngleXU=0 Radius=4 StartAngle=1.5708 EndAngle=4.71239
    g5: ArcOfCircle CenterX=-45.3154 CenterY=182.684 CenterZ=0 NormalX=0 NormalY=0 NormalZ=1 AngleXU=0 Radius=4 StartAngle=4.71239 EndAngle=7.85398
    g6: LineSegment StartX=-50.3154 StartY=178.684 StartZ=0 EndX=-45.3154 EndY=178.684 EndZ=0
    g7: LineSegment StartX=-50.3154 StartY=186.684 StartZ=0 EndX=-45.3154 EndY=186.684 EndZ=0
  constraints (16):
    c: Tangent(g0,g3) = 1.5708
    c: Tangent(g0,g2) = -1.5708
    c: Tangent(g2,g1) = -1.5708
    c: Tangent(g3,g1) = 1.5708
    c: Horizontal(g2)
    c: Coincident(g0,g-5)
    c: Coincident(g-4,g1)
    c: DistanceY(g0,g0) = 5
    c: Tangent(g4,g7) = 1.5708
    c: Tangent(g4,g6) = -1.5708
    c: Tangent(g6,g5) = -1.5708
    c: Tangent(g7,g5) = 1.5708
    c: Horizontal(g6)
    c: Coincident(g4,g0)
    c: DistanceY(g0,g4) = 4
    c: Coincident(g5,g1)
FEATURE [PartDesign::Pad] Pad017
  BaseFeature = -> Pocket034
  Direction = (1,1,1)
  Length = 1
  Length2 = 100
  Placement = pos=(5.21167,0,-39.659) rot=(0,0,1;0rad)
  Profile = -> Sketch044
  Type = 0
FEATURE [PartDesign::Plane] DatumPlane008
  AttachmentOffset = pos=(0,0,7) rot=(0,0,1;0rad)
  Length = 117.546
  MapMode = 5
  Placement = pos=(-1.80165,-1.1e-14,13.7099) rot=(0,-1,0;0.130663rad)
  ResizeMode = 0
  Support = -> [Pad017]
  Width = 242.45
FEATURE [Sketcher::SketchObject] Sketch045
  ExternalGeometry = -> [Pad017]
  FullyConstrained = true
  MapMode = 5
  Placement = pos=(-1.80165,-1.1e-14,13.7099) rot=(0,-1,0;0.130663rad)
  Support = -> [DatumPlane008]
  sketch-geometry (8):
    g0: ArcOfCircle CenterX=-50.3154 CenterY=182.684 CenterZ=0 NormalX=0 NormalY=0 NormalZ=1 AngleXU=0 Radius=5 StartAngle=1.5708 EndAngle=4.71239
    g1: ArcOfCircle CenterX=-45.3154 CenterY=182.684 CenterZ=0 NormalX=0 NormalY=0 NormalZ=1 AngleXU=0 Radius=5 StartAngle=4.71239 EndAngle=7.85398
    g2: LineSegment StartX=-50.3154 StartY=177.684 StartZ=0 EndX=-45.3154 EndY=177.684 EndZ=0
    g3: LineSegment StartX=-50.3154 StartY=187.684 StartZ=0 EndX=-45.3154 EndY=187.684 EndZ=0
    g4: ArcOfCircle CenterX=-50.3154 CenterY=182.684 CenterZ=0 NormalX=0 NormalY=0 NormalZ=1 AngleXU=0 Radius=4 StartAngle=1.5708 EndAngle=4.71239
    g5: ArcOfCircle CenterX=-45.3154 CenterY=182.684 CenterZ=0 NormalX=0 NormalY=0 NormalZ=1 AngleXU=0 Radius=4 StartAngle=4.71239 EndAngle=7.85398
    g6: LineSegment StartX=-50.3154 StartY=178.684 StartZ=0 EndX=-45.3154 EndY=178.684 EndZ=0
    g7: LineSegment StartX=-50.3154 StartY=186.684 StartZ=0 EndX=-45.3154 EndY=186.684 EndZ=0
  constraints (16):
    c: Tangent(g0,g3) = 1.5708
    c: Tangent(g0,g2) = -1.5708
    c: Tangent(g2,g1) = -1.5708
    c: Tangent(g3,g1) = 1.5708
    c: Horizontal(g2)
    c: Coincident(g0,g-5)
    c: Coincident(g-4,g1)
    c: DistanceY(g0,g0) = 5
    c: Tangent(g4,g7) = 1.5708
    c: Tangent(g4,g6) = -1.5708
    c: Tangent(g6,g5) = -1.5708
    c: Tangent(g7,g5) = 1.5708
    c: Horizontal(g6)
    c: Coincident(g4,g0)
    c: Coincident(g5,g1)
    c: DistanceY(g0,g4) = 4
FEATURE [PartDesign::Pad] Pad018
  BaseFeature = -> Pad017
  Direction = (1,1,1)
  Length = 1
  Length2 = 100
  Placement = pos=(5.21167,0,-39.659) rot=(0,0,1;0rad)
  Profile = -> Sketch045
  Type = 0
FEATURE [PartDesign::Chamfer] Chamfer006
  Angle = 45
  Base = -> Pad018 [Edge34,Edge36,Edge40,Edge38]
  BaseFeature = -> Pad018
  ChamferType = 0
  FlipDirection = false
  Placement = pos=(5.21167,0,-39.659) rot=(0,0,1;0rad)
  Size = 0.95
  Size2 = 1
  SupportTransform = false
FEATURE [PartDesign::Chamfer] Chamfer007
  Angle = 45
  Base = -> Chamfer006 [Edge85,Edge88,Edge86,Edge87]
  BaseFeature = -> Chamfer006
  ChamferType = 0
  FlipDirection = false
  Placement = pos=(5.21167,0,-39.659) rot=(0,0,1;0rad)
  Size = 0.95
  Size2 = 1
  SupportTransform = false
FEATURE [PartDesign::Chamfer] Chamfer008
  Angle = 45
  Base = -> Chamfer007 [Edge33,Edge34,Edge35,Edge36]
  BaseFeature = -> Chamfer007
  ChamferType = 0
  FlipDirection = false
  Placement = pos=(5.21167,0,-39.659) rot=(0,0,1;0rad)
  Size = 0.45
  Size2 = 1
  SupportTransform = false
FEATURE [PartDesign::Chamfer] Chamfer009
  Angle = 45
  Base = -> Chamfer008 [Edge26,Edge29,Edge32,Edge31]
  BaseFeature = -> Chamfer008
  ChamferType = 0
  FlipDirection = false
  Placement = pos=(5.21167,0,-39.659) rot=(0,0,1;0rad)
  Size = 0.45
  Size2 = 1
  SupportTransform = false
FEATURE [PartDesign::Fillet] Fillet005
  Base = -> Chamfer009 [Edge91,Edge86,Edge92,Edge89]
  BaseFeature = -> Chamfer009
  Placement = pos=(5.21167,0,-39.659) rot=(0,0,1;0rad)
  Radius = 4
  SupportTransform = false
FEATURE [PartDesign::Body] Body007  label="slider_sock"
  Group = -> [ShapeBinder005,Sketch042,Pad015,Pad016,Fillet004,Chamfer005,Sketch043,Pocket034,DatumPlane007,Sketch044,Pad017,DatumPlane008,Sketch045,Pad018,Chamfer006,Chamfer007,Chamfer008,Chamfer009,Fillet005]
  Origin = -> Origin007
  Tip = -> Fillet005
